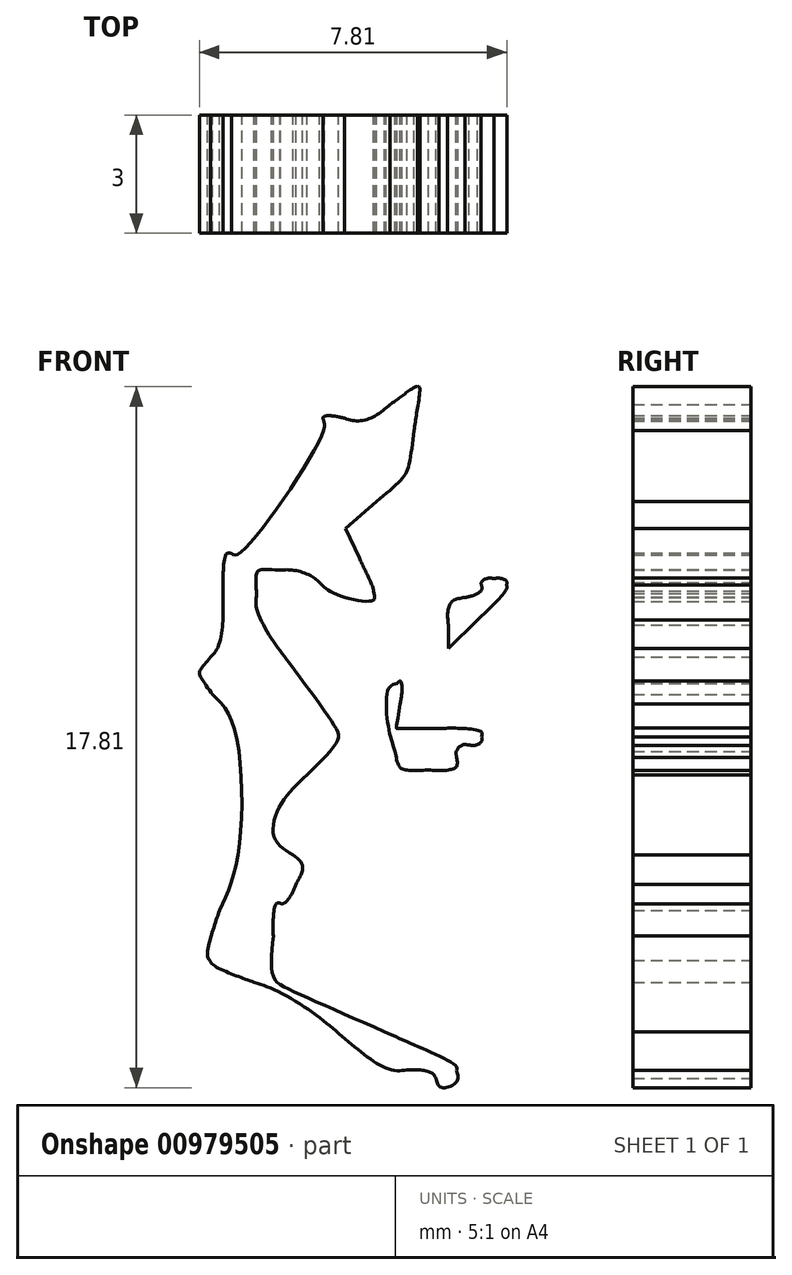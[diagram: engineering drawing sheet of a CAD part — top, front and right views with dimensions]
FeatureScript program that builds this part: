
annotation { "Feature Type Name" : "Feature", "Feature Type Description" : "" }
export const myFeature = defineFeature(function(context is Context, id is Id, definition is map)
    precondition{}
    {
        {
            var Q0;
            Q0=qCreatedBy(makeId("Front.planeOp"),FACE);
            var sketch = newSketch(context, id + "F0", { "sketchPlane" : qUnion([Q0])});
            skLineSegment(sketch, "E0", {"start": v(-32.88, 19.2) * mm, "end": v(-32.1, 20.83) * mm});
            skLineSegment(sketch, "E1", {"start": v(-32.1, 20.83) * mm, "end": v(-32.57, 22.16) * mm});
            skLineSegment(sketch, "E2", {"start": v(-27.5, 16.63) * mm, "end": v(-26.83, 16.28) * mm});
            skLineSegment(sketch, "E3", {"start": v(-26.83, 16.28) * mm, "end": v(-26.97, 16.83) * mm});
            skLineSegment(sketch, "E4", {"start": v(-24.85, 15.67) * mm, "end": v(-25.4, 15.88) * mm});
            skLineSegment(sketch, "E5", {"start": v(-25.4, 15.88) * mm, "end": v(-25.34, 18.4) * mm});
            skLineSegment(sketch, "E6", {"start": v(-1.75, 78.04) * mm, "end": v(-0.2, 79.6) * mm});
            skLineSegment(sketch, "E7", {"start": v(-0.2, 79.6) * mm, "end": v(1.27, 79.6) * mm});
            skLineSegment(sketch, "E8", {"start": v(38.3, 44.26) * mm, "end": v(38.3, 43.17) * mm});
            skLineSegment(sketch, "E9", {"start": v(38.3, 43.17) * mm, "end": v(37.62, 43.24) * mm});
            skLineSegment(sketch, "E10", {"start": v(39.65, -31.25) * mm, "end": v(39.52, -33.83) * mm});
            skLineSegment(sketch, "E11", {"start": v(39.52, -33.83) * mm, "end": v(40.18, -34.42) * mm});
            skLineSegment(sketch, "E12", {"start": v(1.4, 79.08) * mm, "end": v(0.3, 79.22) * mm});
            skLineSegment(sketch, "E13", {"start": v(0.3, 79.22) * mm, "end": v(-1.23, 77.67) * mm});
            skLineSegment(sketch, "E14", {"start": v(-12.51, 69.45) * mm, "end": v(-13.4, 69.45) * mm});
            skLineSegment(sketch, "E15", {"start": v(-13.4, 69.45) * mm, "end": v(-13.27, 67.07) * mm});
            skLineSegment(sketch, "E16", {"start": v(-18.31, 54.9) * mm, "end": v(-18.88, 53.48) * mm});
            skLineSegment(sketch, "E17", {"start": v(-18.88, 53.48) * mm, "end": v(-18.43, 53.1) * mm});
            skLineSegment(sketch, "E18", {"start": v(-20.94, 40.45) * mm, "end": v(-21.55, 40.45) * mm});
            skLineSegment(sketch, "E19", {"start": v(-21.55, 40.45) * mm, "end": v(-21.44, 41.8) * mm});
            skLineSegment(sketch, "E20", {"start": v(-24.47, 43.3) * mm, "end": v(-25.23, 42.61) * mm});
            skLineSegment(sketch, "E21", {"start": v(-25.23, 42.61) * mm, "end": v(-24.8, 41.05) * mm});
            skLineSegment(sketch, "E22", {"start": v(-37.96, -16.18) * mm, "end": v(-37.29, -17.23) * mm});
            skLineSegment(sketch, "E23", {"start": v(-37.29, -17.23) * mm, "end": v(-37.41, -20.41) * mm});
            skLineSegment(sketch, "E24", {"start": v(-30.4, -60.92) * mm, "end": v(-31.42, -62.04) * mm});
            skLineSegment(sketch, "E25", {"start": v(-31.42, -62.04) * mm, "end": v(-30.9, -63.02) * mm});
            skLineSegment(sketch, "E26", {"start": v(-36.35, 33.14) * mm, "end": v(-36.7, 33.88) * mm});
            skLineSegment(sketch, "E27", {"start": v(-36.7, 33.88) * mm, "end": v(-35.92, 34.57) * mm});
            skLineSegment(sketch, "E28", {"start": v(-34.09, 31.43) * mm, "end": v(-34.09, 30.84) * mm});
            skLineSegment(sketch, "E29", {"start": v(-34.09, 30.84) * mm, "end": v(-33.35, 31.56) * mm});
            skFitSpline(sketch, "E30", {"points": [v(-13.45, -80.7) * mm, v(-14.26, -80.4) * mm, v(-15.79, -79.86) * mm, v(-16.84, -79.51) * mm]});
            skFitSpline(sketch, "E31", {"points": [v(-16.84, -79.51) * mm, v(-20.43, -78.33) * mm, v(-20.6, -78.25) * mm, v(-21.55, -77.26) * mm]});
            skFitSpline(sketch, "E32", {"points": [v(-21.55, -77.26) * mm, v(-22.07, -76.72) * mm, v(-23.66, -74.52) * mm, v(-25.09, -72.37) * mm]});
            skFitSpline(sketch, "E33", {"points": [v(-25.09, -72.37) * mm, v(-26.52, -70.21) * mm, v(-28.36, -67.6) * mm, v(-29.19, -66.55) * mm]});
            skFitSpline(sketch, "E34", {"points": [v(-29.19, -66.55) * mm, v(-30.6, -64.76) * mm, v(-31.97, -62.53) * mm, v(-31.97, -62.03) * mm]});
            skFitSpline(sketch, "E35", {"points": [v(-31.97, -62.03) * mm, v(-31.97, -61.91) * mm, v(-31.5, -61.27) * mm, v(-30.92, -60.6) * mm]});
            skFitSpline(sketch, "E36", {"points": [v(-30.92, -60.6) * mm, v(-29.85, -59.39) * mm, v(-29, -57.92) * mm, v(-29, -57.28) * mm]});
            skFitSpline(sketch, "E37", {"points": [v(-29, -57.28) * mm, v(-29, -57.08) * mm, v(-29.34, -56.3) * mm, v(-29.75, -55.53) * mm]});
            skFitSpline(sketch, "E38", {"points": [v(-29.75, -55.53) * mm, v(-30.57, -53.98) * mm, v(-30.63, -53.57) * mm, v(-30.2, -52.72) * mm]});
            skFitSpline(sketch, "E39", {"points": [v(-30.2, -52.72) * mm, v(-29.95, -52.26) * mm, v(-29.92, -51.55) * mm, v(-30.04, -49.29) * mm]});
            skFitSpline(sketch, "E40", {"points": [v(-30.04, -49.29) * mm, v(-30.2, -46.13) * mm, v(-30.12, -46.32) * mm, v(-32.34, -43.6) * mm]});
            skFitSpline(sketch, "E41", {"points": [v(-32.34, -43.6) * mm, v(-32.83, -43) * mm, v(-33.38, -42.01) * mm, v(-33.55, -41.42) * mm]});
            skFitSpline(sketch, "E42", {"points": [v(-33.55, -41.42) * mm, v(-33.73, -40.84) * mm, v(-34.2, -39.94) * mm, v(-34.62, -39.44) * mm]});
            skFitSpline(sketch, "E43", {"points": [v(-34.62, -39.44) * mm, v(-36.03, -37.71) * mm, v(-36.52, -35.97) * mm, v(-35.98, -34.56) * mm]});
            skFitSpline(sketch, "E44", {"points": [v(-35.98, -34.56) * mm, v(-35.86, -34.24) * mm, v(-35.38, -33.57) * mm, v(-34.92, -33.07) * mm]});
            skFitSpline(sketch, "E45", {"points": [v(-34.92, -33.07) * mm, v(-33.97, -32.03) * mm, v(-34, -32.17) * mm, v(-34.37, -30.78) * mm]});
            skFitSpline(sketch, "E46", {"points": [v(-34.37, -30.78) * mm, v(-34.75, -29.38) * mm, v(-35.2, -28.53) * mm, v(-36.46, -26.88) * mm]});
            skFitSpline(sketch, "E47", {"points": [v(-36.46, -26.88) * mm, v(-37.04, -26.13) * mm, v(-37.61, -25.27) * mm, v(-37.73, -24.97) * mm]});
            skFitSpline(sketch, "E48", {"points": [v(-37.73, -24.97) * mm, v(-37.97, -24.39) * mm, v(-38.06, -21.07) * mm, v(-37.9, -18.8) * mm]});
            skFitSpline(sketch, "E49", {"points": [v(-37.9, -18.8) * mm, v(-37.82, -17.55) * mm, v(-37.87, -17.35) * mm, v(-38.39, -16.67) * mm]});
            skFitSpline(sketch, "E50", {"points": [v(-38.39, -16.67) * mm, v(-39.51, -15.19) * mm, v(-39.6, -12.77) * mm, v(-38.72, -7.81) * mm]});
            skFitSpline(sketch, "E51", {"points": [v(-38.72, -7.81) * mm, v(-38.24, -5.14) * mm, v(-38.31, -2.1) * mm, v(-38.87, -1) * mm]});
            skFitSpline(sketch, "E52", {"points": [v(-38.87, -1) * mm, v(-39.1, -0.56) * mm, v(-39.11, -0.29) * mm, v(-38.94, 0.17) * mm]});
            skFitSpline(sketch, "E53", {"points": [v(-38.94, 0.17) * mm, v(-38.62, 1) * mm, v(-38.87, 3.38) * mm, v(-39.5, 5.38) * mm]});
            skFitSpline(sketch, "E54", {"points": [v(-39.5, 5.38) * mm, v(-39.78, 6.29) * mm, v(-40.01, 7.26) * mm, v(-40.01, 7.54) * mm]});
            skFitSpline(sketch, "E55", {"points": [v(-40.01, 7.54) * mm, v(-40.01, 7.83) * mm, v(-39.68, 9.05) * mm, v(-39.27, 10.27) * mm]});
            skFitSpline(sketch, "E56", {"points": [v(-39.27, 10.27) * mm, v(-38.41, 12.85) * mm, v(-38.39, 13.06) * mm, v(-38.96, 13.2) * mm]});
            skFitSpline(sketch, "E57", {"points": [v(-38.96, 13.2) * mm, v(-39.71, 13.4) * mm, v(-39.48, 14.32) * mm, v(-38.38, 15.5) * mm]});
            skFitSpline(sketch, "E58", {"points": [v(-38.38, 15.5) * mm, v(-36.83, 17.16) * mm, v(-35.68, 17.57) * mm, v(-34.74, 16.8) * mm]});
            skFitSpline(sketch, "E59", {"points": [v(-34.74, 16.8) * mm, v(-34.08, 16.26) * mm, v(-32.77, 13.22) * mm, v(-32.66, 11.98) * mm]});
            skFitSpline(sketch, "E60", {"points": [v(-32.66, 11.98) * mm, v(-32.55, 10.86) * mm, v(-32.37, 10.61) * mm, v(-31.6, 10.6) * mm]});
            skFitSpline(sketch, "E61", {"points": [v(-31.6, 10.6) * mm, v(-31, 10.6) * mm, v(-30.96, 11.24) * mm, v(-31.55, 11.77) * mm]});
            skFitSpline(sketch, "E62", {"points": [v(-31.55, 11.77) * mm, v(-31.84, 12.03) * mm, v(-31.97, 12.42) * mm, v(-31.97, 13) * mm]});
            skFitSpline(sketch, "E63", {"points": [v(-31.97, 13) * mm, v(-31.97, 14.32) * mm, v(-32.62, 16.12) * mm, v(-33.18, 16.38) * mm]});
            skFitSpline(sketch, "E64", {"points": [v(-33.18, 16.38) * mm, v(-33.86, 16.69) * mm, v(-33.8, 17.27) * mm, v(-32.88, 19.2) * mm]});
            skFitSpline(sketch, "E65", {"points": [v(-32.57, 22.16) * mm, v(-32.82, 22.9) * mm, v(-33.03, 23.65) * mm, v(-33.03, 23.83) * mm]});
            skFitSpline(sketch, "E66", {"points": [v(-33.03, 23.83) * mm, v(-33.03, 24.1) * mm, v(-33.14, 24.14) * mm, v(-33.5, 24.01) * mm]});
            skFitSpline(sketch, "E67", {"points": [v(-33.5, 24.01) * mm, v(-33.77, 23.92) * mm, v(-34.4, 23.84) * mm, v(-34.93, 23.84) * mm]});
            skFitSpline(sketch, "E68", {"points": [v(-34.93, 23.84) * mm, v(-35.84, 23.83) * mm, v(-35.89, 23.86) * mm, v(-35.95, 24.48) * mm]});
            skFitSpline(sketch, "E69", {"points": [v(-35.95, 24.48) * mm, v(-36.05, 25.55) * mm, v(-34.78, 26.27) * mm, v(-32.78, 26.27) * mm]});
            skFitSpline(sketch, "E70", {"points": [v(-32.78, 26.27) * mm, v(-31.93, 26.27) * mm, v(-31.64, 26.16) * mm, v(-31.1, 25.65) * mm]});
            skFitSpline(sketch, "E71", {"points": [v(-31.1, 25.65) * mm, v(-30.75, 25.3) * mm, v(-30.32, 25.08) * mm, v(-30.15, 25.14) * mm]});
            skFitSpline(sketch, "E72", {"points": [v(-30.15, 25.14) * mm, v(-29.7, 25.31) * mm, v(-29.77, 25.47) * mm, v(-30.7, 26.37) * mm]});
            skFitSpline(sketch, "E73", {"points": [v(-30.7, 26.37) * mm, v(-31.5, 27.15) * mm, v(-31.55, 27.27) * mm, v(-31.55, 28.43) * mm]});
            skFitSpline(sketch, "E74", {"points": [v(-31.55, 28.43) * mm, v(-31.55, 29.6) * mm, v(-31.52, 29.65) * mm, v(-31.02, 29.65) * mm]});
            skFitSpline(sketch, "E75", {"points": [v(-31.02, 29.65) * mm, v(-30.7, 29.65) * mm, v(-30.49, 29.53) * mm, v(-30.49, 29.36) * mm]});
            skFitSpline(sketch, "E76", {"points": [v(-30.49, 29.36) * mm, v(-30.49, 28.94) * mm, v(-28.82, 27.75) * mm, v(-28.24, 27.75) * mm]});
            skFitSpline(sketch, "E77", {"points": [v(-28.24, 27.75) * mm, v(-27.83, 27.75) * mm, v(-27.75, 27.6) * mm, v(-27.62, 26.6) * mm]});
            skFitSpline(sketch, "E78", {"points": [v(-27.62, 26.6) * mm, v(-27.46, 25.26) * mm, v(-27.66, 24.55) * mm, v(-28.57, 23.22) * mm]});
            skFitSpline(sketch, "E79", {"points": [v(-28.57, 23.22) * mm, v(-29.21, 22.29) * mm, v(-29.4, 21.61) * mm, v(-29.02, 21.61) * mm]});
            skFitSpline(sketch, "E80", {"points": [v(-29.02, 21.61) * mm, v(-28.66, 21.61) * mm, v(-28.35, 20.18) * mm, v(-28.49, 19.14) * mm]});
            skFitSpline(sketch, "E81", {"points": [v(-28.49, 19.14) * mm, v(-28.66, 17.84) * mm, v(-28.36, 17.07) * mm, v(-27.5, 16.63) * mm]});
            skFitSpline(sketch, "E82", {"points": [v(-26.97, 16.83) * mm, v(-27.1, 17.33) * mm, v(-27.05, 17.38) * mm, v(-26.5, 17.38) * mm]});
            skFitSpline(sketch, "E83", {"points": [v(-26.5, 17.38) * mm, v(-25.81, 17.38) * mm, v(-25.62, 17.08) * mm, v(-25.62, 16.04) * mm]});
            skFitSpline(sketch, "E84", {"points": [v(-25.62, 16.04) * mm, v(-25.62, 15.5) * mm, v(-25.82, 15.19) * mm, v(-26.56, 14.52) * mm]});
            skFitSpline(sketch, "E85", {"points": [v(-26.56, 14.52) * mm, v(-27.09, 14.05) * mm, v(-27.58, 13.4) * mm, v(-27.66, 13.06) * mm]});
            skFitSpline(sketch, "E86", {"points": [v(-27.66, 13.06) * mm, v(-27.79, 12.49) * mm, v(-27.76, 12.45) * mm, v(-27.3, 12.58) * mm]});
            skFitSpline(sketch, "E87", {"points": [v(-27.3, 12.58) * mm, v(-27.01, 12.65) * mm, v(-26.47, 12.72) * mm, v(-26.09, 12.72) * mm]});
            skFitSpline(sketch, "E88", {"points": [v(-26.09, 12.72) * mm, v(-25.47, 12.72) * mm, v(-25.42, 12.76) * mm, v(-25.61, 13.13) * mm]});
            skFitSpline(sketch, "E89", {"points": [v(-25.61, 13.13) * mm, v(-26.02, 13.88) * mm, v(-25.88, 14.6) * mm, v(-25.31, 14.75) * mm]});
            skFitSpline(sketch, "E90", {"points": [v(-25.31, 14.75) * mm, v(-25.03, 14.82) * mm, v(-24.68, 15.01) * mm, v(-24.55, 15.17) * mm]});
            skFitSpline(sketch, "E91", {"points": [v(-24.55, 15.17) * mm, v(-24.35, 15.4) * mm, v(-24.42, 15.5) * mm, v(-24.85, 15.67) * mm]});
            skFitSpline(sketch, "E92", {"points": [v(-25.34, 18.4) * mm, v(-25.28, 20.49) * mm, v(-25.2, 21.05) * mm, v(-24.84, 21.66) * mm]});
            skFitSpline(sketch, "E93", {"points": [v(-24.84, 21.66) * mm, v(-24.6, 22.07) * mm, v(-24.33, 22.91) * mm, v(-24.25, 23.54) * mm]});
            skFitSpline(sketch, "E94", {"points": [v(-24.25, 23.54) * mm, v(-24.05, 24.98) * mm, v(-23.67, 25.42) * mm, v(-22.64, 25.42) * mm]});
            skFitSpline(sketch, "E95", {"points": [v(-22.64, 25.42) * mm, v(-21.97, 25.42) * mm, v(-21.73, 25.28) * mm, v(-21.09, 24.54) * mm]});
            skFitSpline(sketch, "E96", {"points": [v(-21.09, 24.54) * mm, v(-20.67, 24.05) * mm, v(-20.32, 23.55) * mm, v(-20.32, 23.43) * mm]});
            skFitSpline(sketch, "E97", {"points": [v(-20.32, 23.43) * mm, v(-20.3, 22.93) * mm, v(-19.5, 25.15) * mm, v(-19.5, 25.74) * mm]});
            skFitSpline(sketch, "E98", {"points": [v(-19.5, 25.74) * mm, v(-19.48, 26.68) * mm, v(-19.75, 27) * mm, v(-20.27, 26.68) * mm]});
            skFitSpline(sketch, "E99", {"points": [v(-20.27, 26.68) * mm, v(-20.84, 26.32) * mm, v(-23.7, 26.75) * mm, v(-24.99, 27.38) * mm]});
            skFitSpline(sketch, "E100", {"points": [v(-24.99, 27.38) * mm, v(-26.7, 28.23) * mm, v(-27.27, 29.95) * mm, v(-26.55, 32.07) * mm]});
            skFitSpline(sketch, "E101", {"points": [v(-26.55, 32.07) * mm, v(-26.23, 33) * mm, v(-26.23, 33.13) * mm, v(-26.58, 33.9) * mm]});
            skFitSpline(sketch, "E102", {"points": [v(-26.58, 33.9) * mm, v(-27.04, 34.91) * mm, v(-26.9, 36) * mm, v(-26.2, 36.92) * mm]});
            skFitSpline(sketch, "E103", {"points": [v(-26.2, 36.92) * mm, v(-24.96, 38.54) * mm, v(-24.76, 39.42) * mm, v(-25.3, 40.73) * mm]});
            skFitSpline(sketch, "E104", {"points": [v(-25.3, 40.73) * mm, v(-25.48, 41.15) * mm, v(-25.62, 41.87) * mm, v(-25.62, 42.33) * mm]});
            skFitSpline(sketch, "E105", {"points": [v(-25.62, 42.33) * mm, v(-25.62, 43.02) * mm, v(-25.5, 43.25) * mm, v(-24.99, 43.62) * mm]});
            skFitSpline(sketch, "E106", {"points": [v(-24.99, 43.62) * mm, v(-24.64, 43.87) * mm, v(-24.35, 44.26) * mm, v(-24.35, 44.48) * mm]});
            skFitSpline(sketch, "E107", {"points": [v(-24.35, 44.48) * mm, v(-24.35, 45.6) * mm, v(-22.43, 46.16) * mm, v(-21.62, 45.29) * mm]});
            skFitSpline(sketch, "E108", {"points": [v(-21.62, 45.29) * mm, v(-21.1, 44.74) * mm, v(-20.66, 42.78) * mm, v(-20.82, 41.8) * mm]});
            skFitSpline(sketch, "E109", {"points": [v(-20.82, 41.8) * mm, v(-20.95, 40.98) * mm, v(-20.5, 40.8) * mm, v(-20.12, 41.5) * mm]});
            skFitSpline(sketch, "E110", {"points": [v(-20.12, 41.5) * mm, v(-20, 41.74) * mm, v(-19.7, 41.93) * mm, v(-19.48, 41.93) * mm]});
            skFitSpline(sketch, "E111", {"points": [v(-19.48, 41.93) * mm, v(-19.2, 41.93) * mm, v(-19.03, 42.12) * mm, v(-18.95, 42.51) * mm]});
            skFitSpline(sketch, "E112", {"points": [v(-18.95, 42.51) * mm, v(-18.9, 42.83) * mm, v(-18.75, 43.5) * mm, v(-18.63, 44) * mm]});
            skFitSpline(sketch, "E113", {"points": [v(-18.63, 44) * mm, v(-18.15, 46.1) * mm, v(-18.46, 46.83) * mm, v(-19.95, 47.1) * mm]});
            skFitSpline(sketch, "E114", {"points": [v(-19.95, 47.1) * mm, v(-21.37, 47.35) * mm, v(-21.68, 48.31) * mm, v(-21.02, 50.45) * mm]});
            skFitSpline(sketch, "E115", {"points": [v(-21.02, 50.45) * mm, v(-20.67, 51.58) * mm, v(-20.6, 51.66) * mm, v(-20, 51.67) * mm]});
            skFitSpline(sketch, "E116", {"points": [v(-20, 51.67) * mm, v(-19.64, 51.67) * mm, v(-19.17, 51.8) * mm, v(-18.94, 51.97) * mm]});
            skFitSpline(sketch, "E117", {"points": [v(-18.94, 51.97) * mm, v(-18.56, 52.25) * mm, v(-18.55, 52.28) * mm, v(-18.9, 52.67) * mm]});
            skFitSpline(sketch, "E118", {"points": [v(-18.9, 52.67) * mm, v(-19.36, 53.18) * mm, v(-19.37, 53.99) * mm, v(-18.93, 55) * mm]});
            skFitSpline(sketch, "E119", {"points": [v(-18.93, 55) * mm, v(-18.26, 56.57) * mm, v(-18.22, 56.96) * mm, v(-18.55, 58.71) * mm]});
            skFitSpline(sketch, "E120", {"points": [v(-18.55, 58.71) * mm, v(-19.05, 61.35) * mm, v(-18.66, 63.1) * mm, v(-17.57, 63.1) * mm]});
            skFitSpline(sketch, "E121", {"points": [v(-17.57, 63.1) * mm, v(-17.13, 63.1) * mm, v(-16.93, 62.86) * mm, v(-16.62, 61.94) * mm]});
            skFitSpline(sketch, "E122", {"points": [v(-16.62, 61.94) * mm, v(-16.19, 60.62) * mm, v(-15.25, 61.36) * mm, v(-15.25, 63.03) * mm]});
            skFitSpline(sketch, "E123", {"points": [v(-15.25, 63.03) * mm, v(-15.25, 63.72) * mm, v(-15.21, 63.77) * mm, v(-14.72, 63.65) * mm]});
            skFitSpline(sketch, "E124", {"points": [v(-14.72, 63.65) * mm, v(-13.88, 63.44) * mm, v(-13.7, 64.21) * mm, v(-13.86, 67.25) * mm]});
            skFitSpline(sketch, "E125", {"points": [v(-13.86, 67.25) * mm, v(-14.01, 70.15) * mm, v(-14.06, 70.07) * mm, v(-12.21, 70.08) * mm]});
            skFitSpline(sketch, "E126", {"points": [v(-12.21, 70.08) * mm, v(-11.52, 70.08) * mm, v(-11.25, 70.23) * mm, v(-10.4, 71.12) * mm]});
            skFitSpline(sketch, "E127", {"points": [v(-10.4, 71.12) * mm, v(-9.38, 72.18) * mm, v(-9.03, 72.34) * mm, v(-6.52, 72.84) * mm]});
            skFitSpline(sketch, "E128", {"points": [v(-6.52, 72.84) * mm, v(-4.93, 73.15) * mm, v(-4.21, 73.78) * mm, v(-3.7, 75.27) * mm]});
            skFitSpline(sketch, "E129", {"points": [v(-3.7, 75.27) * mm, v(-3.38, 76.2) * mm, v(-2.96, 76.8) * mm, v(-1.75, 78.04) * mm]});
            skFitSpline(sketch, "E130", {"points": [v(1.27, 79.6) * mm, v(2.66, 79.6) * mm, v(2.79, 79.65) * mm, v(3.57, 80.36) * mm]});
            skFitSpline(sketch, "E131", {"points": [v(3.57, 80.36) * mm, v(4.72, 81.4) * mm, v(5.62, 81.51) * mm, v(6.84, 80.8) * mm]});
            skFitSpline(sketch, "E132", {"points": [v(6.84, 80.8) * mm, v(7.4, 80.48) * mm, v(8.11, 80.24) * mm, v(8.56, 80.24) * mm]});
            skFitSpline(sketch, "E133", {"points": [v(8.56, 80.24) * mm, v(9.65, 80.24) * mm, v(10.66, 79.76) * mm, v(12.03, 78.58) * mm]});
            skFitSpline(sketch, "E134", {"points": [v(12.03, 78.58) * mm, v(12.68, 78.02) * mm, v(13.76, 77.21) * mm, v(14.43, 76.8) * mm]});
            skFitSpline(sketch, "E135", {"points": [v(14.43, 76.8) * mm, v(16.07, 75.75) * mm, v(16.3, 75.23) * mm, v(16.26, 72.68) * mm]});
            skFitSpline(sketch, "E136", {"points": [v(16.26, 72.68) * mm, v(16.21, 70.3) * mm, v(16.3, 70.06) * mm, v(17.99, 67.97) * mm]});
            skFitSpline(sketch, "E137", {"points": [v(17.99, 67.97) * mm, v(19.34, 66.28) * mm, v(19.58, 65.73) * mm, v(19.78, 63.84) * mm]});
            skFitSpline(sketch, "E138", {"points": [v(19.78, 63.84) * mm, v(19.97, 61.97) * mm, v(20.1, 61.75) * mm, v(21.2, 61.28) * mm]});
            skFitSpline(sketch, "E139", {"points": [v(21.2, 61.28) * mm, v(21.95, 60.97) * mm, v(22.77, 60.9) * mm, v(25.95, 60.87) * mm]});
            skFitSpline(sketch, "E140", {"points": [v(25.95, 60.87) * mm, v(29.47, 60.83) * mm, v(29.87, 60.8) * mm, v(30.78, 60.35) * mm]});
            skFitSpline(sketch, "E141", {"points": [v(30.78, 60.35) * mm, v(31.33, 60.09) * mm, v(31.82, 59.71) * mm, v(31.88, 59.53) * mm]});
            skFitSpline(sketch, "E142", {"points": [v(31.88, 59.53) * mm, v(32.1, 58.78) * mm, v(32.32, 58.58) * mm, v(33.34, 58.19) * mm]});
            skFitSpline(sketch, "E143", {"points": [v(33.34, 58.19) * mm, v(35, 57.54) * mm, v(35.47, 56.96) * mm, v(35.61, 55.41) * mm]});
            skFitSpline(sketch, "E144", {"points": [v(35.61, 55.41) * mm, v(35.68, 54.7) * mm, v(35.93, 53.67) * mm, v(36.17, 53.15) * mm]});
            skFitSpline(sketch, "E145", {"points": [v(36.17, 53.15) * mm, v(36.4, 52.63) * mm, v(36.6, 51.94) * mm, v(36.6, 51.62) * mm]});
            skFitSpline(sketch, "E146", {"points": [v(36.6, 51.62) * mm, v(36.6, 51.3) * mm, v(36.8, 50.55) * mm, v(37.02, 49.93) * mm]});
            skFitSpline(sketch, "E147", {"points": [v(37.02, 49.93) * mm, v(37.7, 48.08) * mm, v(38.3, 45.42) * mm, v(38.3, 44.26) * mm]});
            skFitSpline(sketch, "E148", {"points": [v(37.62, 43.24) * mm, v(36.87, 43.31) * mm, v(36.86, 43.33) * mm, v(36.05, 46.9) * mm]});
            skFitSpline(sketch, "E149", {"points": [v(36.05, 46.9) * mm, v(35.75, 48.23) * mm, v(35.65, 48.45) * mm, v(35.6, 47.92) * mm]});
            skFitSpline(sketch, "E150", {"points": [v(35.6, 47.92) * mm, v(35.56, 47.55) * mm, v(35.72, 46.61) * mm, v(35.96, 45.84) * mm]});
            skFitSpline(sketch, "E151", {"points": [v(35.96, 45.84) * mm, v(36.2, 45.06) * mm, v(36.4, 44.16) * mm, v(36.4, 43.83) * mm]});
            skFitSpline(sketch, "E152", {"points": [v(36.4, 43.83) * mm, v(36.4, 42.72) * mm, v(36.23, 42.57) * mm, v(35.04, 42.57) * mm]});
            skFitSpline(sketch, "E153", {"points": [v(35.04, 42.57) * mm, v(34.35, 42.57) * mm, v(33.78, 42.44) * mm, v(33.53, 42.23) * mm]});
            skFitSpline(sketch, "E154", {"points": [v(33.53, 42.23) * mm, v(33.14, 41.92) * mm, v(33.15, 41.9) * mm, v(33.78, 42.01) * mm]});
            skFitSpline(sketch, "E155", {"points": [v(33.78, 42.01) * mm, v(34.37, 42.1) * mm, v(34.48, 42.05) * mm, v(34.7, 41.5) * mm]});
            skFitSpline(sketch, "E156", {"points": [v(34.7, 41.5) * mm, v(35.23, 40.23) * mm, v(34.46, 39.89) * mm, v(32.77, 40.66) * mm]});
            skFitSpline(sketch, "E157", {"points": [v(32.77, 40.66) * mm, v(30, 41.91) * mm, v(30.46, 40.26) * mm, v(33.3, 38.77) * mm]});
            skFitSpline(sketch, "E158", {"points": [v(33.3, 38.77) * mm, v(34.7, 38.04) * mm, v(35.03, 37.98) * mm, v(35.2, 38.44) * mm]});
            skFitSpline(sketch, "E159", {"points": [v(35.2, 38.44) * mm, v(35.4, 38.97) * mm, v(36.94, 38.86) * mm, v(37.34, 38.29) * mm]});
            skFitSpline(sketch, "E160", {"points": [v(37.34, 38.29) * mm, v(37.8, 37.64) * mm, v(37.75, 36.5) * mm, v(37.25, 35.69) * mm]});
            skFitSpline(sketch, "E161", {"points": [v(37.25, 35.69) * mm, v(37.01, 35.31) * mm, v(36.68, 34.6) * mm, v(36.5, 34.09) * mm]});
            skFitSpline(sketch, "E162", {"points": [v(36.5, 34.09) * mm, v(36.07, 32.87) * mm, v(35.62, 32.4) * mm, v(34.86, 32.4) * mm]});
            skFitSpline(sketch, "E163", {"points": [v(34.86, 32.4) * mm, v(34.06, 32.4) * mm, v(32.85, 32.98) * mm, v(32.57, 33.5) * mm]});
            skFitSpline(sketch, "E164", {"points": [v(32.57, 33.5) * mm, v(32.35, 33.9) * mm, v(32.37, 33.91) * mm, v(33.4, 34.23) * mm]});
            skFitSpline(sketch, "E165", {"points": [v(33.4, 34.23) * mm, v(33.55, 34.27) * mm, v(33.64, 34.43) * mm, v(33.6, 34.58) * mm]});
            skFitSpline(sketch, "E166", {"points": [v(33.6, 34.58) * mm, v(33.47, 34.97) * mm, v(32.1, 35.02) * mm, v(31.26, 34.66) * mm]});
            skFitSpline(sketch, "E167", {"points": [v(31.26, 34.66) * mm, v(30.63, 34.4) * mm, v(30.54, 34.27) * mm, v(30.63, 33.8) * mm]});
            skFitSpline(sketch, "E168", {"points": [v(30.63, 33.8) * mm, v(30.71, 33.37) * mm, v(30.83, 33.27) * mm, v(31.13, 33.37) * mm]});
            skFitSpline(sketch, "E169", {"points": [v(31.13, 33.37) * mm, v(31.68, 33.54) * mm, v(31.8, 33.13) * mm, v(31.57, 31.7) * mm]});
            skFitSpline(sketch, "E170", {"points": [v(31.57, 31.7) * mm, v(31.47, 31.04) * mm, v(31.4, 30.5) * mm, v(31.43, 30.5) * mm]});
            skFitSpline(sketch, "E171", {"points": [v(31.43, 30.5) * mm, v(31.46, 30.5) * mm, v(31.82, 30.65) * mm, v(32.25, 30.82) * mm]});
            skFitSpline(sketch, "E172", {"points": [v(32.25, 30.82) * mm, v(33.01, 31.14) * mm, v(33.02, 31.14) * mm, v(33.26, 30.56) * mm]});
            skFitSpline(sketch, "E173", {"points": [v(33.26, 30.56) * mm, v(33.39, 30.24) * mm, v(33.5, 29.43) * mm, v(33.52, 28.77) * mm]});
            skFitSpline(sketch, "E174", {"points": [v(33.52, 28.77) * mm, v(33.55, 27.14) * mm, v(33.03, 26.57) * mm, v(31.4, 26.43) * mm]});
            skFitSpline(sketch, "E175", {"points": [v(31.4, 26.43) * mm, v(29.99, 26.32) * mm, v(29.27, 25.83) * mm, v(28.59, 24.5) * mm]});
            skFitSpline(sketch, "E176", {"points": [v(28.59, 24.5) * mm, v(28.09, 23.52) * mm, v(28.09, 23.5) * mm, v(28.46, 22.8) * mm]});
            skFitSpline(sketch, "E177", {"points": [v(28.46, 22.8) * mm, v(29.02, 21.76) * mm, v(28.8, 20.5) * mm, v(27.76, 18.77) * mm]});
            skFitSpline(sketch, "E178", {"points": [v(27.76, 18.77) * mm, v(26.26, 16.28) * mm, v(26.34, 15.6) * mm, v(28.5, 12.89) * mm]});
            skFitSpline(sketch, "E179", {"points": [v(28.5, 12.89) * mm, v(30.07, 10.9) * mm, v(30.64, 9.85) * mm, v(31.32, 7.7) * mm]});
            skFitSpline(sketch, "E180", {"points": [v(31.32, 7.7) * mm, v(31.79, 6.2) * mm, v(31.8, 6.14) * mm, v(31.41, 5.73) * mm]});
            skFitSpline(sketch, "E181", {"points": [v(31.41, 5.73) * mm, v(31.08, 5.36) * mm, v(31.06, 5.2) * mm, v(31.28, 4.6) * mm]});
            skFitSpline(sketch, "E182", {"points": [v(31.28, 4.6) * mm, v(31.65, 3.58) * mm, v(31.59, 2.92) * mm, v(31, 1.59) * mm]});
            skFitSpline(sketch, "E183", {"points": [v(31, 1.59) * mm, v(30.4, 0.22) * mm, v(30.37, 0) * mm, v(30.73, -0.98) * mm]});
            skFitSpline(sketch, "E184", {"points": [v(30.73, -0.98) * mm, v(30.96, -1.6) * mm, v(30.93, -1.79) * mm, v(30.48, -2.62) * mm]});
            skFitSpline(sketch, "E185", {"points": [v(30.48, -2.62) * mm, v(29.76, -3.92) * mm, v(30.03, -4.4) * mm, v(31.97, -5.39) * mm]});
            skFitSpline(sketch, "E186", {"points": [v(31.97, -5.39) * mm, v(33.32, -6.07) * mm, v(33.55, -6.12) * mm, v(34.1, -5.9) * mm]});
            skFitSpline(sketch, "E187", {"points": [v(34.1, -5.9) * mm, v(34.89, -5.57) * mm, v(35.48, -5.74) * mm, v(36.67, -6.64) * mm]});
            skFitSpline(sketch, "E188", {"points": [v(36.67, -6.64) * mm, v(37.21, -7.06) * mm, v(37.94, -7.45) * mm, v(38.28, -7.52) * mm]});
            skFitSpline(sketch, "E189", {"points": [v(38.28, -7.52) * mm, v(38.74, -7.61) * mm, v(38.97, -7.82) * mm, v(39.14, -8.29) * mm]});
            skFitSpline(sketch, "E190", {"points": [v(39.14, -8.29) * mm, v(39.46, -9.22) * mm, v(39.43, -9.36) * mm, v(38.73, -10.24) * mm]});
            skFitSpline(sketch, "E191", {"points": [v(38.73, -10.24) * mm, v(37.95, -11.22) * mm, v(37.9, -12.13) * mm, v(38.57, -13.12) * mm]});
            skFitSpline(sketch, "E192", {"points": [v(38.57, -13.12) * mm, v(38.94, -13.67) * mm, v(39.23, -13.86) * mm, v(39.79, -13.91) * mm]});
            skFitSpline(sketch, "E193", {"points": [v(39.79, -13.91) * mm, v(40.2, -13.95) * mm, v(40.6, -14.1) * mm, v(40.68, -14.23) * mm]});
            skFitSpline(sketch, "E194", {"points": [v(40.68, -14.23) * mm, v(40.98, -14.7) * mm, v(40.84, -15.58) * mm, v(40.4, -15.98) * mm]});
            skFitSpline(sketch, "E195", {"points": [v(40.4, -15.98) * mm, v(40.04, -16.3) * mm, v(39.97, -16.56) * mm, v(40.05, -17.26) * mm]});
            skFitSpline(sketch, "E196", {"points": [v(40.05, -17.26) * mm, v(40.14, -18.03) * mm, v(40.09, -18.17) * mm, v(39.65, -18.37) * mm]});
            skFitSpline(sketch, "E197", {"points": [v(39.65, -18.37) * mm, v(39.06, -18.64) * mm, v(39.03, -18.9) * mm, v(39.5, -20) * mm]});
            skFitSpline(sketch, "E198", {"points": [v(39.5, -20) * mm, v(39.77, -20.67) * mm, v(39.83, -21.57) * mm, v(39.81, -24.74) * mm]});
            skFitSpline(sketch, "E199", {"points": [v(39.81, -24.74) * mm, v(39.8, -26.9) * mm, v(39.73, -29.82) * mm, v(39.65, -31.25) * mm]});
            skFitSpline(sketch, "E200", {"points": [v(40.18, -34.42) * mm, v(40.54, -34.74) * mm, v(40.84, -35.18) * mm, v(40.84, -35.41) * mm]});
            skFitSpline(sketch, "E201", {"points": [v(40.84, -35.41) * mm, v(40.84, -36.27) * mm, v(39.96, -37.65) * mm, v(38.92, -38.41) * mm]});
            skFitSpline(sketch, "E202", {"points": [v(38.92, -38.41) * mm, v(37.63, -39.36) * mm, v(37.28, -40) * mm, v(37.05, -41.89) * mm]});
            skFitSpline(sketch, "E203", {"points": [v(37.05, -41.89) * mm, v(36.94, -42.7) * mm, v(36.66, -43.77) * mm, v(36.42, -44.27) * mm]});
            skFitSpline(sketch, "E204", {"points": [v(36.42, -44.27) * mm, v(35.96, -45.22) * mm, v(33.78, -47.87) * mm, v(31.3, -50.5) * mm]});
            skFitSpline(sketch, "E205", {"points": [v(31.3, -50.5) * mm, v(29.02, -52.92) * mm, v(27.8, -55.66) * mm, v(27.2, -59.77) * mm]});
            skFitSpline(sketch, "E206", {"points": [v(27.2, -59.77) * mm, v(26.85, -62.13) * mm, v(26.75, -62.37) * mm, v(25.14, -65) * mm]});
            skFitSpline(sketch, "E207", {"points": [v(25.14, -65) * mm, v(24.58, -65.91) * mm, v(24.35, -66.6) * mm, v(24.16, -67.9) * mm]});
            skFitSpline(sketch, "E208", {"points": [v(24.16, -67.9) * mm, v(23.88, -69.93) * mm, v(23.36, -71.03) * mm, v(22.29, -71.92) * mm]});
            skFitSpline(sketch, "E209", {"points": [v(22.29, -71.92) * mm, v(21.43, -72.63) * mm, v(19.94, -73.22) * mm, v(19, -73.22) * mm]});
            skFitSpline(sketch, "E210", {"points": [v(19, -73.22) * mm, v(18.6, -73.22) * mm, v(18.4, -73.32) * mm, v(18.4, -73.56) * mm]});
            skFitSpline(sketch, "E211", {"points": [v(18.4, -73.56) * mm, v(18.4, -73.75) * mm, v(18.21, -74.22) * mm, v(17.97, -74.6) * mm]});
            skFitSpline(sketch, "E212", {"points": [v(17.97, -74.6) * mm, v(17.57, -75.26) * mm, v(17.56, -75.35) * mm, v(17.87, -76.08) * mm]});
            skFitSpline(sketch, "E213", {"points": [v(17.87, -76.08) * mm, v(18.34, -77.22) * mm, v(18.3, -77.38) * mm, v(17.14, -78.58) * mm]});
            skFitSpline(sketch, "E214", {"points": [v(17.14, -78.58) * mm, v(16.56, -79.18) * mm, v(15.87, -79.93) * mm, v(15.6, -80.25) * mm]});
            skFitSpline(sketch, "E215", {"points": [v(15.6, -80.25) * mm, v(15.34, -80.56) * mm, v(14.86, -80.88) * mm, v(14.54, -80.96) * mm]});
            skFitSpline(sketch, "E216", {"points": [v(14.54, -80.96) * mm, v(14.03, -81.08) * mm, v(13.96, -81.03) * mm, v(13.96, -80.56) * mm]});
            skFitSpline(sketch, "E217", {"points": [v(13.96, -80.56) * mm, v(13.96, -80.25) * mm, v(13.75, -79.86) * mm, v(13.47, -79.63) * mm]});
            skFitSpline(sketch, "E218", {"points": [v(13.47, -79.63) * mm, v(12.33, -78.73) * mm, v(12.3, -77.45) * mm, v(13.44, -77.45) * mm]});
            skFitSpline(sketch, "E219", {"points": [v(13.44, -77.45) * mm, v(14.2, -77.45) * mm, v(15.11, -76) * mm, v(14.94, -75.07) * mm]});
            skFitSpline(sketch, "E220", {"points": [v(14.94, -75.07) * mm, v(14.87, -74.7) * mm, v(14.75, -74.02) * mm, v(14.67, -73.57) * mm]});
            skFitSpline(sketch, "E221", {"points": [v(14.67, -73.57) * mm, v(14.58, -73.02) * mm, v(14.45, -72.8) * mm, v(14.25, -72.88) * mm]});
            skFitSpline(sketch, "E222", {"points": [v(14.25, -72.88) * mm, v(14.1, -72.94) * mm, v(13.13, -72.88) * mm, v(12.11, -72.76) * mm]});
            skFitSpline(sketch, "E223", {"points": [v(12.11, -72.76) * mm, v(10.8, -72.6) * mm, v(10.12, -72.4) * mm, v(9.8, -72.1) * mm]});
            skFitSpline(sketch, "E224", {"points": [v(9.8, -72.1) * mm, v(9.32, -71.67) * mm, v(8.88, -71.75) * mm, v(8.88, -72.28) * mm]});
            skFitSpline(sketch, "E225", {"points": [v(8.88, -72.28) * mm, v(8.88, -72.66) * mm, v(8.5, -72.65) * mm, v(7.82, -72.26) * mm]});
            skFitSpline(sketch, "E226", {"points": [v(7.82, -72.26) * mm, v(7.11, -71.86) * mm, v(5.83, -71.87) * mm, v(4.94, -72.29) * mm]});
            skFitSpline(sketch, "E227", {"points": [v(4.94, -72.29) * mm, v(4.16, -72.66) * mm, v(4.18, -72.61) * mm, v(4.14, -74.27) * mm]});
            skFitSpline(sketch, "E228", {"points": [v(4.14, -74.27) * mm, v(4.12, -75.43) * mm, v(4.11, -75.44) * mm, v(3.17, -75.91) * mm]});
            skFitSpline(sketch, "E229", {"points": [v(3.17, -75.91) * mm, v(2.65, -76.18) * mm, v(1.84, -76.77) * mm, v(1.36, -77.24) * mm]});
            skFitSpline(sketch, "E230", {"points": [v(1.36, -77.24) * mm, v(0.68, -77.91) * mm, v(-0.19, -78.37) * mm, v(-2.67, -79.37) * mm]});
            skFitSpline(sketch, "E231", {"points": [v(-2.67, -79.37) * mm, v(-6.5, -80.92) * mm, v(-7.82, -81.25) * mm, v(-10.17, -81.25) * mm]});
            skFitSpline(sketch, "E232", {"points": [v(-10.17, -81.25) * mm, v(-11.59, -81.25) * mm, v(-12.28, -81.13) * mm, v(-13.45, -80.7) * mm]});
            skFitSpline(sketch, "E233", {"points": [v(-6.84, -80.3) * mm, v(-6.29, -80.14) * mm, v(-4.56, -79.5) * mm, v(-3, -78.88) * mm]});
            skFitSpline(sketch, "E234", {"points": [v(-3, -78.88) * mm, v(-0.66, -77.96) * mm, v(0.05, -77.57) * mm, v(1.08, -76.65) * mm]});
            skFitSpline(sketch, "E235", {"points": [v(1.08, -76.65) * mm, v(1.77, -76.04) * mm, v(2.46, -75.54) * mm, v(2.62, -75.54) * mm]});
            skFitSpline(sketch, "E236", {"points": [v(2.62, -75.54) * mm, v(2.78, -75.54) * mm, v(3.12, -75.37) * mm, v(3.38, -75.16) * mm]});
            skFitSpline(sketch, "E237", {"points": [v(3.38, -75.16) * mm, v(3.8, -74.81) * mm, v(3.83, -74.72) * mm, v(3.59, -73.93) * mm]});
            skFitSpline(sketch, "E238", {"points": [v(3.59, -73.93) * mm, v(3.4, -73.28) * mm, v(3.39, -72.96) * mm, v(3.57, -72.61) * mm]});
            skFitSpline(sketch, "E239", {"points": [v(3.57, -72.61) * mm, v(4.07, -71.69) * mm, v(6.12, -71.11) * mm, v(7.53, -71.5) * mm]});
            skFitSpline(sketch, "E240", {"points": [v(7.53, -71.5) * mm, v(8.17, -71.68) * mm, v(8.4, -71.66) * mm, v(8.68, -71.41) * mm]});
            skFitSpline(sketch, "E241", {"points": [v(8.68, -71.41) * mm, v(9.15, -70.98) * mm, v(9.64, -71.02) * mm, v(10.13, -71.54) * mm]});
            skFitSpline(sketch, "E242", {"points": [v(10.13, -71.54) * mm, v(10.44, -71.88) * mm, v(10.95, -72.03) * mm, v(12.2, -72.17) * mm]});
            skFitSpline(sketch, "E243", {"points": [v(12.2, -72.17) * mm, v(13.1, -72.28) * mm, v(14, -72.32) * mm, v(14.17, -72.26) * mm]});
            skFitSpline(sketch, "E244", {"points": [v(14.17, -72.26) * mm, v(14.75, -72.09) * mm, v(15.04, -72.5) * mm, v(15.33, -73.91) * mm]});
            skFitSpline(sketch, "E245", {"points": [v(15.33, -73.91) * mm, v(15.54, -74.89) * mm, v(15.57, -75.53) * mm, v(15.43, -76.04) * mm]});
            skFitSpline(sketch, "E246", {"points": [v(15.43, -76.04) * mm, v(15.14, -77.06) * mm, v(14.45, -77.87) * mm, v(13.85, -77.87) * mm]});
            skFitSpline(sketch, "E247", {"points": [v(13.85, -77.87) * mm, v(13.06, -77.87) * mm, v(13.01, -78.27) * mm, v(13.7, -79) * mm]});
            skFitSpline(sketch, "E248", {"points": [v(13.7, -79) * mm, v(14.06, -79.37) * mm, v(14.38, -79.86) * mm, v(14.43, -80.1) * mm]});
            skFitSpline(sketch, "E249", {"points": [v(14.43, -80.1) * mm, v(14.5, -80.48) * mm, v(14.55, -80.47) * mm, v(15.03, -79.9) * mm]});
            skFitSpline(sketch, "E250", {"points": [v(15.03, -79.9) * mm, v(15.31, -79.57) * mm, v(16.02, -78.83) * mm, v(16.6, -78.28) * mm]});
            skFitSpline(sketch, "E251", {"points": [v(16.6, -78.28) * mm, v(17.64, -77.28) * mm, v(17.65, -77.26) * mm, v(17.4, -76.55) * mm]});
            skFitSpline(sketch, "E252", {"points": [v(17.4, -76.55) * mm, v(17.05, -75.6) * mm, v(17.07, -74.87) * mm, v(17.45, -74.37) * mm]});
            skFitSpline(sketch, "E253", {"points": [v(17.45, -74.37) * mm, v(17.62, -74.14) * mm, v(17.76, -73.7) * mm, v(17.76, -73.4) * mm]});
            skFitSpline(sketch, "E254", {"points": [v(17.76, -73.4) * mm, v(17.77, -72.89) * mm, v(17.86, -72.83) * mm, v(18.88, -72.7) * mm]});
            skFitSpline(sketch, "E255", {"points": [v(18.88, -72.7) * mm, v(19.5, -72.62) * mm, v(20.47, -72.3) * mm, v(21.04, -71.99) * mm]});
            skFitSpline(sketch, "E256", {"points": [v(21.04, -71.99) * mm, v(22.45, -71.22) * mm, v(23.22, -70.08) * mm, v(23.5, -68.35) * mm]});
            skFitSpline(sketch, "E257", {"points": [v(23.5, -68.35) * mm, v(23.9, -65.9) * mm, v(24.16, -65.2) * mm, v(25.1, -63.87) * mm]});
            skFitSpline(sketch, "E258", {"points": [v(25.1, -63.87) * mm, v(26.18, -62.33) * mm, v(26.35, -61.85) * mm, v(26.67, -59.46) * mm]});
            skFitSpline(sketch, "E259", {"points": [v(26.67, -59.46) * mm, v(26.98, -57.13) * mm, v(27.93, -54.18) * mm, v(28.89, -52.58) * mm]});
            skFitSpline(sketch, "E260", {"points": [v(28.89, -52.58) * mm, v(29.3, -51.88) * mm, v(30.25, -50.69) * mm, v(31, -49.93) * mm]});
            skFitSpline(sketch, "E261", {"points": [v(31, -49.93) * mm, v(33.26, -47.61) * mm, v(35.36, -45.01) * mm, v(35.9, -43.88) * mm]});
            skFitSpline(sketch, "E262", {"points": [v(35.9, -43.88) * mm, v(36.17, -43.28) * mm, v(36.49, -42.11) * mm, v(36.6, -41.27) * mm]});
            skFitSpline(sketch, "E263", {"points": [v(36.6, -41.27) * mm, v(36.81, -39.5) * mm, v(37.06, -39.06) * mm, v(38.37, -38.07) * mm]});
            skFitSpline(sketch, "E264", {"points": [v(38.37, -38.07) * mm, v(39.26, -37.4) * mm, v(40.2, -36.1) * mm, v(40.2, -35.57) * mm]});
            skFitSpline(sketch, "E265", {"points": [v(40.2, -35.57) * mm, v(40.2, -35.45) * mm, v(39.98, -35.11) * mm, v(39.7, -34.83) * mm]});
            skFitSpline(sketch, "E266", {"points": [v(39.7, -34.83) * mm, v(38.98, -34.12) * mm, v(38.86, -33.18) * mm, v(39.13, -30.68) * mm]});
            skFitSpline(sketch, "E267", {"points": [v(39.13, -30.68) * mm, v(39.26, -29.5) * mm, v(39.36, -26.93) * mm, v(39.36, -24.95) * mm]});
            skFitSpline(sketch, "E268", {"points": [v(39.36, -24.95) * mm, v(39.36, -21.87) * mm, v(39.3, -21.22) * mm, v(38.94, -20.3) * mm]});
            skFitSpline(sketch, "E269", {"points": [v(38.94, -20.3) * mm, v(38.39, -18.9) * mm, v(38.4, -18.51) * mm, v(39.04, -18) * mm]});
            skFitSpline(sketch, "E270", {"points": [v(39.04, -18) * mm, v(39.45, -17.69) * mm, v(39.57, -17.4) * mm, v(39.57, -16.76) * mm]});
            skFitSpline(sketch, "E271", {"points": [v(39.57, -16.76) * mm, v(39.57, -16.2) * mm, v(39.7, -15.8) * mm, v(39.97, -15.56) * mm]});
            skFitSpline(sketch, "E272", {"points": [v(39.97, -15.56) * mm, v(40.59, -15) * mm, v(40.32, -14.37) * mm, v(39.46, -14.37) * mm]});
            skFitSpline(sketch, "E273", {"points": [v(39.46, -14.37) * mm, v(38.38, -14.37) * mm, v(37.67, -13.4) * mm, v(37.67, -11.9) * mm]});
            skFitSpline(sketch, "E274", {"points": [v(37.67, -11.9) * mm, v(37.67, -10.72) * mm, v(37.93, -9.95) * mm, v(38.44, -9.65) * mm]});
            skFitSpline(sketch, "E275", {"points": [v(38.44, -9.65) * mm, v(39.04, -9.3) * mm, v(38.7, -8.02) * mm, v(38, -8.02) * mm]});
            skFitSpline(sketch, "E276", {"points": [v(38, -8.02) * mm, v(37.74, -8.02) * mm, v(37, -7.64) * mm, v(36.34, -7.18) * mm]});
            skFitSpline(sketch, "E277", {"points": [v(36.34, -7.18) * mm, v(35.18, -6.34) * mm, v(34.43, -6.12) * mm, v(34.18, -6.54) * mm]});
            skFitSpline(sketch, "E278", {"points": [v(34.18, -6.54) * mm, v(34.1, -6.66) * mm, v(33.87, -6.75) * mm, v(33.65, -6.75) * mm]});
            skFitSpline(sketch, "E279", {"points": [v(33.65, -6.75) * mm, v(33.07, -6.75) * mm, v(30.08, -5.09) * mm, v(29.83, -4.63) * mm]});
            skFitSpline(sketch, "E280", {"points": [v(29.83, -4.63) * mm, v(29.5, -4) * mm, v(29.6, -2.89) * mm, v(30.04, -2.22) * mm]});
            skFitSpline(sketch, "E281", {"points": [v(30.04, -2.22) * mm, v(30.4, -1.66) * mm, v(30.41, -1.54) * mm, v(30.14, -1.01) * mm]});
            skFitSpline(sketch, "E282", {"points": [v(30.14, -1.01) * mm, v(29.71, -0.19) * mm, v(29.76, 0.38) * mm, v(30.37, 1.68) * mm]});
            skFitSpline(sketch, "E283", {"points": [v(30.37, 1.68) * mm, v(30.96, 2.95) * mm, v(31, 3.5) * mm, v(30.65, 4.7) * mm]});
            skFitSpline(sketch, "E284", {"points": [v(30.65, 4.7) * mm, v(30.44, 5.4) * mm, v(30.46, 5.58) * mm, v(30.78, 5.93) * mm]});
            skFitSpline(sketch, "E285", {"points": [v(30.78, 5.93) * mm, v(31.13, 6.33) * mm, v(31.13, 6.4) * mm, v(30.68, 7.79) * mm]});
            skFitSpline(sketch, "E286", {"points": [v(30.68, 7.79) * mm, v(30.01, 9.8) * mm, v(29.64, 10.47) * mm, v(28.1, 12.43) * mm]});
            skFitSpline(sketch, "E287", {"points": [v(28.1, 12.43) * mm, v(27.35, 13.37) * mm, v(26.61, 14.44) * mm, v(26.46, 14.8) * mm]});
            skFitSpline(sketch, "E288", {"points": [v(26.46, 14.8) * mm, v(26, 15.95) * mm, v(26.28, 17.5) * mm, v(27.26, 19.16) * mm]});
            skFitSpline(sketch, "E289", {"points": [v(27.26, 19.16) * mm, v(28.4, 21.1) * mm, v(28.53, 21.7) * mm, v(27.93, 22.5) * mm]});
            skFitSpline(sketch, "E290", {"points": [v(27.93, 22.5) * mm, v(27.4, 23.23) * mm, v(27.46, 23.77) * mm, v(28.28, 25.17) * mm]});
            skFitSpline(sketch, "E291", {"points": [v(28.28, 25.17) * mm, v(28.94, 26.3) * mm, v(29.89, 26.9) * mm, v(31.02, 26.9) * mm]});
            skFitSpline(sketch, "E292", {"points": [v(31.02, 26.9) * mm, v(31.6, 26.9) * mm, v(32.1, 27.06) * mm, v(32.48, 27.36) * mm]});
            skFitSpline(sketch, "E293", {"points": [v(32.48, 27.36) * mm, v(33, 27.78) * mm, v(33.05, 27.91) * mm, v(32.96, 28.95) * mm]});
            skFitSpline(sketch, "E294", {"points": [v(32.96, 28.95) * mm, v(32.91, 29.57) * mm, v(32.82, 30.13) * mm, v(32.76, 30.19) * mm]});
            skFitSpline(sketch, "E295", {"points": [v(32.76, 30.19) * mm, v(32.7, 30.25) * mm, v(32.3, 30.15) * mm, v(31.89, 29.97) * mm]});
            skFitSpline(sketch, "E296", {"points": [v(31.89, 29.97) * mm, v(31.46, 29.8) * mm, v(31.06, 29.65) * mm, v(30.98, 29.65) * mm]});
            skFitSpline(sketch, "E297", {"points": [v(30.98, 29.65) * mm, v(30.9, 29.65) * mm, v(30.9, 30.37) * mm, v(30.97, 31.24) * mm]});
            skFitSpline(sketch, "E298", {"points": [v(30.97, 31.24) * mm, v(31.1, 32.73) * mm, v(31.07, 32.83) * mm, v(30.68, 32.83) * mm]});
            skFitSpline(sketch, "E299", {"points": [v(30.68, 32.83) * mm, v(30.45, 32.83) * mm, v(30.26, 32.97) * mm, v(30.26, 33.15) * mm]});
            skFitSpline(sketch, "E300", {"points": [v(30.26, 33.15) * mm, v(30.26, 33.32) * mm, v(30.16, 33.46) * mm, v(30.05, 33.46) * mm]});
            skFitSpline(sketch, "E301", {"points": [v(30.05, 33.46) * mm, v(29.69, 33.46) * mm, v(29.82, 34.44) * mm, v(30.23, 34.81) * mm]});
            skFitSpline(sketch, "E302", {"points": [v(30.23, 34.81) * mm, v(30.44, 35) * mm, v(31.16, 35.28) * mm, v(31.83, 35.42) * mm]});
            skFitSpline(sketch, "E303", {"points": [v(31.83, 35.42) * mm, v(32.85, 35.63) * mm, v(33.13, 35.62) * mm, v(33.6, 35.36) * mm]});
            skFitSpline(sketch, "E304", {"points": [v(33.6, 35.36) * mm, v(34.37, 34.93) * mm, v(34.48, 34.05) * mm, v(33.82, 33.73) * mm]});
            skFitSpline(sketch, "E305", {"points": [v(33.82, 33.73) * mm, v(33.34, 33.51) * mm, v(33.35, 33.5) * mm, v(34.15, 33.16) * mm]});
            skFitSpline(sketch, "E306", {"points": [v(34.15, 33.16) * mm, v(34.9, 32.83) * mm, v(34.99, 32.83) * mm, v(35.36, 33.17) * mm]});
            skFitSpline(sketch, "E307", {"points": [v(35.36, 33.17) * mm, v(35.58, 33.37) * mm, v(35.76, 33.64) * mm, v(35.76, 33.77) * mm]});
            skFitSpline(sketch, "E308", {"points": [v(35.76, 33.77) * mm, v(35.76, 33.9) * mm, v(36.1, 34.7) * mm, v(36.5, 35.56) * mm]});
            skFitSpline(sketch, "E309", {"points": [v(36.5, 35.56) * mm, v(37.29, 37.18) * mm, v(37.3, 37.75) * mm, v(36.61, 38.12) * mm]});
            skFitSpline(sketch, "E310", {"points": [v(36.61, 38.12) * mm, v(36.14, 38.38) * mm, v(35.55, 38.19) * mm, v(35.55, 37.78) * mm]});
            skFitSpline(sketch, "E311", {"points": [v(35.55, 37.78) * mm, v(35.55, 36.66) * mm, v(30.79, 39.12) * mm, v(30.36, 40.45) * mm]});
            skFitSpline(sketch, "E312", {"points": [v(30.36, 40.45) * mm, v(30.3, 40.68) * mm, v(30.34, 41.05) * mm, v(30.47, 41.29) * mm]});
            skFitSpline(sketch, "E313", {"points": [v(30.47, 41.29) * mm, v(30.77, 41.86) * mm, v(31.55, 41.83) * mm, v(33.01, 41.2) * mm]});
            skFitSpline(sketch, "E314", {"points": [v(33.01, 41.2) * mm, v(34.25, 40.67) * mm, v(34.4, 40.66) * mm, v(34.2, 41.18) * mm]});
            skFitSpline(sketch, "E315", {"points": [v(34.2, 41.18) * mm, v(34.13, 41.4) * mm, v(33.81, 41.5) * mm, v(33.34, 41.5) * mm]});
            skFitSpline(sketch, "E316", {"points": [v(33.34, 41.5) * mm, v(32.48, 41.5) * mm, v(32.37, 41.83) * mm, v(32.97, 42.57) * mm]});
            skFitSpline(sketch, "E317", {"points": [v(32.97, 42.57) * mm, v(33.3, 42.96) * mm, v(33.56, 43.04) * mm, v(34.54, 43.04) * mm]});
            skFitSpline(sketch, "E318", {"points": [v(34.54, 43.04) * mm, v(36.05, 43.02) * mm, v(36.12, 43.25) * mm, v(35.4, 45.67) * mm]});
            skFitSpline(sketch, "E319", {"points": [v(35.4, 45.67) * mm, v(34.98, 47.1) * mm, v(34.9, 47.7) * mm, v(35.01, 48.62) * mm]});
            skFitSpline(sketch, "E320", {"points": [v(35.01, 48.62) * mm, v(35.1, 49.37) * mm, v(35.26, 49.76) * mm, v(35.45, 49.76) * mm]});
            skFitSpline(sketch, "E321", {"points": [v(35.45, 49.76) * mm, v(35.79, 49.76) * mm, v(36.46, 48.04) * mm, v(36.81, 46.27) * mm]});
            skFitSpline(sketch, "E322", {"points": [v(36.81, 46.27) * mm, v(37.15, 44.53) * mm, v(37.45, 43.62) * mm, v(37.68, 43.62) * mm]});
            skFitSpline(sketch, "E323", {"points": [v(37.68, 43.62) * mm, v(37.8, 43.62) * mm, v(37.88, 43.84) * mm, v(37.88, 44.1) * mm]});
            skFitSpline(sketch, "E324", {"points": [v(37.88, 44.1) * mm, v(37.88, 44.74) * mm, v(36.88, 48.83) * mm, v(36.6, 49.36) * mm]});
            skFitSpline(sketch, "E325", {"points": [v(36.6, 49.36) * mm, v(36.47, 49.6) * mm, v(36.29, 50.3) * mm, v(36.19, 50.92) * mm]});
            skFitSpline(sketch, "E326", {"points": [v(36.19, 50.92) * mm, v(36.09, 51.54) * mm, v(35.8, 52.48) * mm, v(35.57, 53.01) * mm]});
            skFitSpline(sketch, "E327", {"points": [v(35.57, 53.01) * mm, v(35.31, 53.57) * mm, v(35.13, 54.41) * mm, v(35.13, 55.03) * mm]});
            skFitSpline(sketch, "E328", {"points": [v(35.13, 55.03) * mm, v(35.13, 56.37) * mm, v(34.52, 57.14) * mm, v(33.05, 57.66) * mm]});
            skFitSpline(sketch, "E329", {"points": [v(33.05, 57.66) * mm, v(31.97, 58.05) * mm, v(31.44, 58.5) * mm, v(31.02, 59.34) * mm]});
            skFitSpline(sketch, "E330", {"points": [v(31.02, 59.34) * mm, v(30.64, 60.08) * mm, v(29.4, 60.31) * mm, v(25.6, 60.34) * mm]});
            skFitSpline(sketch, "E331", {"points": [v(25.6, 60.34) * mm, v(21.36, 60.37) * mm, v(20.2, 60.66) * mm, v(19.62, 61.83) * mm]});
            skFitSpline(sketch, "E332", {"points": [v(19.62, 61.83) * mm, v(19.42, 62.24) * mm, v(19.25, 63.05) * mm, v(19.25, 63.63) * mm]});
            skFitSpline(sketch, "E333", {"points": [v(19.25, 63.63) * mm, v(19.24, 64.97) * mm, v(18.71, 66.14) * mm, v(17.39, 67.73) * mm]});
            skFitSpline(sketch, "E334", {"points": [v(17.39, 67.73) * mm, v(15.95, 69.45) * mm, v(15.56, 70.55) * mm, v(15.72, 72.4) * mm]});
            skFitSpline(sketch, "E335", {"points": [v(15.72, 72.4) * mm, v(15.89, 74.42) * mm, v(15.61, 75.26) * mm, v(14.57, 75.97) * mm]});
            skFitSpline(sketch, "E336", {"points": [v(14.57, 75.97) * mm, v(13.8, 76.48) * mm, v(12.94, 77.13) * mm, v(10.52, 78.96) * mm]});
            skFitSpline(sketch, "E337", {"points": [v(10.52, 78.96) * mm, v(9.93, 79.4) * mm, v(9.37, 79.6) * mm, v(8.4, 79.72) * mm]});
            skFitSpline(sketch, "E338", {"points": [v(8.4, 79.72) * mm, v(7.67, 79.8) * mm, v(6.83, 80.05) * mm, v(6.52, 80.27) * mm]});
            skFitSpline(sketch, "E339", {"points": [v(6.52, 80.27) * mm, v(5.73, 80.83) * mm, v(4.99, 80.76) * mm, v(4.18, 80.06) * mm]});
            skFitSpline(sketch, "E340", {"points": [v(4.18, 80.06) * mm, v(3.06, 79.09) * mm, v(2.62, 78.93) * mm, v(1.4, 79.08) * mm]});
            skFitSpline(sketch, "E341", {"points": [v(-1.23, 77.67) * mm, v(-2.35, 76.53) * mm, v(-2.88, 75.8) * mm, v(-3.2, 74.95) * mm]});
            skFitSpline(sketch, "E342", {"points": [v(-3.2, 74.95) * mm, v(-3.44, 74.31) * mm, v(-3.84, 73.58) * mm, v(-4.08, 73.32) * mm]});
            skFitSpline(sketch, "E343", {"points": [v(-4.08, 73.32) * mm, v(-4.6, 72.75) * mm, v(-5.86, 72.28) * mm, v(-7.31, 72.1) * mm]});
            skFitSpline(sketch, "E344", {"points": [v(-7.31, 72.1) * mm, v(-8.5, 71.94) * mm, v(-9.16, 71.58) * mm, v(-9.92, 70.68) * mm]});
            skFitSpline(sketch, "E345", {"points": [v(-9.92, 70.68) * mm, v(-10.62, 69.85) * mm, v(-11.46, 69.45) * mm, v(-12.51, 69.45) * mm]});
            skFitSpline(sketch, "E346", {"points": [v(-13.27, 67.07) * mm, v(-13.12, 64.4) * mm, v(-13.35, 63.34) * mm, v(-14.15, 63) * mm]});
            skFitSpline(sketch, "E347", {"points": [v(-14.15, 63) * mm, v(-14.41, 62.88) * mm, v(-14.68, 62.54) * mm, v(-14.74, 62.25) * mm]});
            skFitSpline(sketch, "E348", {"points": [v(-14.74, 62.25) * mm, v(-14.95, 61.27) * mm, v(-15.22, 60.8) * mm, v(-15.67, 60.66) * mm]});
            skFitSpline(sketch, "E349", {"points": [v(-15.67, 60.66) * mm, v(-16.3, 60.47) * mm, v(-17.15, 61.07) * mm, v(-17.15, 61.71) * mm]});
            skFitSpline(sketch, "E350", {"points": [v(-17.15, 61.71) * mm, v(-17.15, 62.4) * mm, v(-17.57, 62.62) * mm, v(-17.95, 62.12) * mm]});
            skFitSpline(sketch, "E351", {"points": [v(-17.95, 62.12) * mm, v(-18.25, 61.72) * mm, v(-18.24, 60.86) * mm, v(-17.87, 57.55) * mm]});
            skFitSpline(sketch, "E352", {"points": [v(-17.87, 57.55) * mm, v(-17.76, 56.53) * mm, v(-17.83, 56.11) * mm, v(-18.31, 54.9) * mm]});
            skFitSpline(sketch, "E353", {"points": [v(-18.43, 53.1) * mm, v(-18.09, 52.84) * mm, v(-18, 52.61) * mm, v(-18.12, 52.26) * mm]});
            skFitSpline(sketch, "E354", {"points": [v(-18.12, 52.26) * mm, v(-18.35, 51.5) * mm, v(-18.6, 51.29) * mm, v(-19.44, 51.14) * mm]});
            skFitSpline(sketch, "E355", {"points": [v(-19.44, 51.14) * mm, v(-20.16, 51.02) * mm, v(-20.25, 50.92) * mm, v(-20.59, 49.92) * mm]});
            skFitSpline(sketch, "E356", {"points": [v(-20.59, 49.92) * mm, v(-21.07, 48.49) * mm, v(-20.79, 47.82) * mm, v(-19.64, 47.63) * mm]});
            skFitSpline(sketch, "E357", {"points": [v(-19.64, 47.63) * mm, v(-18.7, 47.48) * mm, v(-18.1, 46.98) * mm, v(-17.9, 46.22) * mm]});
            skFitSpline(sketch, "E358", {"points": [v(-17.9, 46.22) * mm, v(-17.82, 45.92) * mm, v(-17.92, 44.77) * mm, v(-18.12, 43.68) * mm]});
            skFitSpline(sketch, "E359", {"points": [v(-18.12, 43.68) * mm, v(-18.44, 41.9) * mm, v(-18.54, 41.66) * mm, v(-19.03, 41.44) * mm]});
            skFitSpline(sketch, "E360", {"points": [v(-19.03, 41.44) * mm, v(-19.33, 41.3) * mm, v(-19.75, 41.02) * mm, v(-19.96, 40.82) * mm]});
            skFitSpline(sketch, "E361", {"points": [v(-19.96, 40.82) * mm, v(-20.16, 40.62) * mm, v(-20.6, 40.45) * mm, v(-20.94, 40.45) * mm]});
            skFitSpline(sketch, "E362", {"points": [v(-21.44, 41.8) * mm, v(-21.32, 43.27) * mm, v(-21.6, 44.43) * mm, v(-22.21, 44.98) * mm]});
            skFitSpline(sketch, "E363", {"points": [v(-22.21, 44.98) * mm, v(-22.54, 45.28) * mm, v(-22.7, 45.3) * mm, v(-23.16, 45.08) * mm]});
            skFitSpline(sketch, "E364", {"points": [v(-23.16, 45.08) * mm, v(-23.48, 44.93) * mm, v(-23.72, 44.65) * mm, v(-23.72, 44.41) * mm]});
            skFitSpline(sketch, "E365", {"points": [v(-23.72, 44.41) * mm, v(-23.72, 44.19) * mm, v(-24.06, 43.69) * mm, v(-24.47, 43.3) * mm]});
            skFitSpline(sketch, "E366", {"points": [v(-24.8, 41.05) * mm, v(-24.28, 39.2) * mm, v(-24.4, 38.43) * mm, v(-25.38, 37) * mm]});
            skFitSpline(sketch, "E367", {"points": [v(-25.38, 37) * mm, v(-26.38, 35.55) * mm, v(-26.52, 35.03) * mm, v(-26.15, 34.3) * mm]});
            skFitSpline(sketch, "E368", {"points": [v(-26.15, 34.3) * mm, v(-25.74, 33.52) * mm, v(-25.75, 32.64) * mm, v(-26.17, 31.34) * mm]});
            skFitSpline(sketch, "E369", {"points": [v(-26.17, 31.34) * mm, v(-26.5, 30.34) * mm, v(-26.5, 30.27) * mm, v(-26.05, 29.35) * mm]});
            skFitSpline(sketch, "E370", {"points": [v(-26.05, 29.35) * mm, v(-25.45, 28.12) * mm, v(-24.64, 27.64) * mm, v(-22.5, 27.27) * mm]});
            skFitSpline(sketch, "E371", {"points": [v(-22.5, 27.27) * mm, v(-21.03, 27.01) * mm, v(-20.71, 27.01) * mm, v(-20.51, 27.25) * mm]});
            skFitSpline(sketch, "E372", {"points": [v(-20.51, 27.25) * mm, v(-20.2, 27.62) * mm, v(-19.6, 27.62) * mm, v(-19.29, 27.24) * mm]});
            skFitSpline(sketch, "E373", {"points": [v(-19.29, 27.24) * mm, v(-18.74, 26.58) * mm, v(-18.77, 25.45) * mm, v(-19.37, 23.93) * mm]});
            skFitSpline(sketch, "E374", {"points": [v(-19.37, 23.93) * mm, v(-19.7, 23.08) * mm, v(-20.07, 22.46) * mm, v(-20.24, 22.46) * mm]});
            skFitSpline(sketch, "E375", {"points": [v(-20.24, 22.46) * mm, v(-20.4, 22.46) * mm, v(-20.54, 22.54) * mm, v(-20.54, 22.65) * mm]});
            skFitSpline(sketch, "E376", {"points": [v(-20.54, 22.65) * mm, v(-20.54, 23.08) * mm, v(-22.27, 25) * mm, v(-22.65, 25) * mm]});
            skFitSpline(sketch, "E377", {"points": [v(-22.65, 25) * mm, v(-23.23, 25) * mm, v(-23.72, 24.2) * mm, v(-23.72, 23.22) * mm]});
            skFitSpline(sketch, "E378", {"points": [v(-23.72, 23.22) * mm, v(-23.72, 22.72) * mm, v(-23.92, 22.04) * mm, v(-24.24, 21.5) * mm]});
            skFitSpline(sketch, "E379", {"points": [v(-24.24, 21.5) * mm, v(-24.66, 20.79) * mm, v(-24.75, 20.34) * mm, v(-24.74, 19.26) * mm]});
            skFitSpline(sketch, "E380", {"points": [v(-24.74, 19.26) * mm, v(-24.72, 18.51) * mm, v(-24.78, 17.69) * mm, v(-24.86, 17.43) * mm]});
            skFitSpline(sketch, "E381", {"points": [v(-24.86, 17.43) * mm, v(-25.08, 16.75) * mm, v(-24.82, 16.1) * mm, v(-24.33, 16.1) * mm]});
            skFitSpline(sketch, "E382", {"points": [v(-24.33, 16.1) * mm, v(-23.36, 16.1) * mm, v(-23.83, 14.55) * mm, v(-24.88, 14.3) * mm]});
            skFitSpline(sketch, "E383", {"points": [v(-24.88, 14.3) * mm, v(-25.3, 14.18) * mm, v(-25.36, 14.09) * mm, v(-25.2, 13.77) * mm]});
            skFitSpline(sketch, "E384", {"points": [v(-25.2, 13.77) * mm, v(-24.96, 13.34) * mm, v(-24.91, 12.23) * mm, v(-25.11, 12.03) * mm]});
            skFitSpline(sketch, "E385", {"points": [v(-25.11, 12.03) * mm, v(-25.18, 11.96) * mm, v(-25.46, 11.98) * mm, v(-25.73, 12.09) * mm]});
            skFitSpline(sketch, "E386", {"points": [v(-25.73, 12.09) * mm, v(-26.03, 12.2) * mm, v(-26.5, 12.18) * mm, v(-26.98, 12.04) * mm]});
            skFitSpline(sketch, "E387", {"points": [v(-26.98, 12.04) * mm, v(-28.78, 11.48) * mm, v(-28.79, 13.48) * mm, v(-26.99, 14.98) * mm]});
            skFitSpline(sketch, "E388", {"points": [v(-26.99, 14.98) * mm, v(-26.47, 15.42) * mm, v(-26.04, 15.92) * mm, v(-26.04, 16.09) * mm]});
            skFitSpline(sketch, "E389", {"points": [v(-26.04, 16.09) * mm, v(-26.04, 16.33) * mm, v(-26.1, 16.35) * mm, v(-26.3, 16.15) * mm]});
            skFitSpline(sketch, "E390", {"points": [v(-26.3, 16.15) * mm, v(-26.76, 15.69) * mm, v(-27.73, 15.86) * mm, v(-28.39, 16.52) * mm]});
            skFitSpline(sketch, "E391", {"points": [v(-28.39, 16.52) * mm, v(-28.98, 17.1) * mm, v(-29, 17.22) * mm, v(-29, 18.97) * mm]});
            skFitSpline(sketch, "E392", {"points": [v(-29, 18.97) * mm, v(-29, 20.63) * mm, v(-29.05, 20.82) * mm, v(-29.43, 20.91) * mm]});
            skFitSpline(sketch, "E393", {"points": [v(-29.43, 20.91) * mm, v(-30.19, 21.11) * mm, v(-29.94, 22.23) * mm, v(-28.69, 24.26) * mm]});
            skFitSpline(sketch, "E394", {"points": [v(-28.69, 24.26) * mm, v(-27.87, 25.58) * mm, v(-28, 27.33) * mm, v(-28.9, 27.33) * mm]});
            skFitSpline(sketch, "E395", {"points": [v(-28.9, 27.33) * mm, v(-29.17, 27.33) * mm, v(-29.7, 27.61) * mm, v(-30.07, 27.96) * mm]});
            skFitSpline(sketch, "E396", {"points": [v(-30.07, 27.96) * mm, v(-30.87, 28.71) * mm, v(-31.12, 28.76) * mm, v(-31.12, 28.14) * mm]});
            skFitSpline(sketch, "E397", {"points": [v(-31.12, 28.14) * mm, v(-31.12, 27.9) * mm, v(-30.7, 27.23) * mm, v(-30.17, 26.67) * mm]});
            skFitSpline(sketch, "E398", {"points": [v(-30.17, 26.67) * mm, v(-29.12, 25.55) * mm, v(-29.07, 25.4) * mm, v(-29.55, 24.9) * mm]});
            skFitSpline(sketch, "E399", {"points": [v(-29.55, 24.9) * mm, v(-30.1, 24.36) * mm, v(-30.96, 24.5) * mm, v(-31.6, 25.23) * mm]});
            skFitSpline(sketch, "E400", {"points": [v(-31.6, 25.23) * mm, v(-32.15, 25.85) * mm, v(-32.25, 25.88) * mm, v(-33.19, 25.74) * mm]});
            skFitSpline(sketch, "E401", {"points": [v(-33.19, 25.74) * mm, v(-34.37, 25.57) * mm, v(-35.26, 25.15) * mm, v(-35.43, 24.68) * mm]});
            skFitSpline(sketch, "E402", {"points": [v(-35.43, 24.68) * mm, v(-35.6, 24.23) * mm, v(-35.14, 24.08) * mm, v(-34.43, 24.35) * mm]});
            skFitSpline(sketch, "E403", {"points": [v(-34.43, 24.35) * mm, v(-34.1, 24.48) * mm, v(-33.54, 24.57) * mm, v(-33.15, 24.57) * mm]});
            skFitSpline(sketch, "E404", {"points": [v(-33.15, 24.57) * mm, v(-32.54, 24.57) * mm, v(-32.46, 24.5) * mm, v(-32.44, 24) * mm]});
            skFitSpline(sketch, "E405", {"points": [v(-32.44, 24) * mm, v(-32.43, 23.67) * mm, v(-32.27, 23.06) * mm, v(-32.1, 22.62) * mm]});
            skFitSpline(sketch, "E406", {"points": [v(-32.1, 22.62) * mm, v(-31.58, 21.42) * mm, v(-31.67, 20.28) * mm, v(-32.4, 18.86) * mm]});
            skFitSpline(sketch, "E407", {"points": [v(-32.4, 18.86) * mm, v(-33.14, 17.4) * mm, v(-33.17, 17.05) * mm, v(-32.63, 16.75) * mm]});
            skFitSpline(sketch, "E408", {"points": [v(-32.63, 16.75) * mm, v(-32.1, 16.47) * mm, v(-31.55, 14.82) * mm, v(-31.55, 13.54) * mm]});
            skFitSpline(sketch, "E409", {"points": [v(-31.55, 13.54) * mm, v(-31.55, 12.77) * mm, v(-31.45, 12.46) * mm, v(-31.11, 12.23) * mm]});
            skFitSpline(sketch, "E410", {"points": [v(-31.11, 12.23) * mm, v(-30.88, 12.06) * mm, v(-30.63, 11.6) * mm, v(-30.56, 11.18) * mm]});
            skFitSpline(sketch, "E411", {"points": [v(-30.56, 11.18) * mm, v(-30.46, 10.56) * mm, v(-30.52, 10.4) * mm, v(-30.91, 10.18) * mm]});
            skFitSpline(sketch, "E412", {"points": [v(-30.91, 10.18) * mm, v(-31.53, 9.85) * mm, v(-32.75, 10.1) * mm, v(-33.03, 10.6) * mm]});
            skFitSpline(sketch, "E413", {"points": [v(-33.03, 10.6) * mm, v(-33.14, 10.82) * mm, v(-33.25, 11.41) * mm, v(-33.26, 11.91) * mm]});
            skFitSpline(sketch, "E414", {"points": [v(-33.26, 11.91) * mm, v(-33.27, 12.53) * mm, v(-33.55, 13.4) * mm, v(-34.16, 14.63) * mm]});
            skFitSpline(sketch, "E415", {"points": [v(-34.16, 14.63) * mm, v(-34.97, 16.28) * mm, v(-35.1, 16.43) * mm, v(-35.72, 16.5) * mm]});
            skFitSpline(sketch, "E416", {"points": [v(-35.72, 16.5) * mm, v(-36.31, 16.55) * mm, v(-36.58, 16.38) * mm, v(-37.73, 15.23) * mm]});
            skFitSpline(sketch, "E417", {"points": [v(-37.73, 15.23) * mm, v(-38.93, 14.04) * mm, v(-39.01, 13.9) * mm, v(-38.59, 13.83) * mm]});
            skFitSpline(sketch, "E418", {"points": [v(-38.59, 13.83) * mm, v(-38.17, 13.76) * mm, v(-38.1, 13.62) * mm, v(-38.11, 12.76) * mm]});
            skFitSpline(sketch, "E419", {"points": [v(-38.11, 12.76) * mm, v(-38.12, 12.21) * mm, v(-38.4, 10.97) * mm, v(-38.75, 9.98) * mm]});
            skFitSpline(sketch, "E420", {"points": [v(-38.75, 9.98) * mm, v(-39.51, 7.8) * mm, v(-39.52, 7.37) * mm, v(-38.83, 5.2) * mm]});
            skFitSpline(sketch, "E421", {"points": [v(-38.83, 5.2) * mm, v(-38.38, 3.8) * mm, v(-38.3, 3.15) * mm, v(-38.32, 1.4) * mm]});
            skFitSpline(sketch, "E422", {"points": [v(-38.32, 1.4) * mm, v(-38.34, 0.23) * mm, v(-38.26, -1.1) * mm, v(-38.13, -1.57) * mm]});
            skFitSpline(sketch, "E423", {"points": [v(-38.13, -1.57) * mm, v(-37.77, -2.92) * mm, v(-37.86, -6.07) * mm, v(-38.34, -8.88) * mm]});
            skFitSpline(sketch, "E424", {"points": [v(-38.34, -8.88) * mm, v(-38.63, -10.58) * mm, v(-38.76, -12.12) * mm, v(-38.71, -13.3) * mm]});
            skFitSpline(sketch, "E425", {"points": [v(-38.71, -13.3) * mm, v(-38.65, -14.92) * mm, v(-38.56, -15.24) * mm, v(-37.96, -16.18) * mm]});
            skFitSpline(sketch, "E426", {"points": [v(-37.41, -20.41) * mm, v(-37.55, -24.06) * mm, v(-37.43, -24.65) * mm, v(-36.22, -26.18) * mm]});
            skFitSpline(sketch, "E427", {"points": [v(-36.22, -26.18) * mm, v(-34.5, -28.36) * mm, v(-33.66, -30.2) * mm, v(-33.66, -31.8) * mm]});
            skFitSpline(sketch, "E428", {"points": [v(-33.66, -31.8) * mm, v(-33.66, -32.5) * mm, v(-33.82, -32.8) * mm, v(-34.62, -33.66) * mm]});
            skFitSpline(sketch, "E429", {"points": [v(-34.62, -33.66) * mm, v(-35.46, -34.56) * mm, v(-35.57, -34.79) * mm, v(-35.57, -35.64) * mm]});
            skFitSpline(sketch, "E430", {"points": [v(-35.57, -35.64) * mm, v(-35.57, -36.85) * mm, v(-35.16, -37.86) * mm, v(-34.2, -38.96) * mm]});
            skFitSpline(sketch, "E431", {"points": [v(-34.2, -38.96) * mm, v(-33.8, -39.44) * mm, v(-33.28, -40.4) * mm, v(-33.04, -41.1) * mm]});
            skFitSpline(sketch, "E432", {"points": [v(-33.04, -41.1) * mm, v(-32.76, -41.93) * mm, v(-32.24, -42.8) * mm, v(-31.56, -43.59) * mm]});
            skFitSpline(sketch, "E433", {"points": [v(-31.56, -43.59) * mm, v(-29.64, -45.8) * mm, v(-29.61, -45.88) * mm, v(-29.6, -49.55) * mm]});
            skFitSpline(sketch, "E434", {"points": [v(-29.6, -49.55) * mm, v(-29.59, -51.33) * mm, v(-29.65, -53.1) * mm, v(-29.74, -53.47) * mm]});
            skFitSpline(sketch, "E435", {"points": [v(-29.74, -53.47) * mm, v(-29.87, -54.05) * mm, v(-29.78, -54.34) * mm, v(-29.2, -55.24) * mm]});
            skFitSpline(sketch, "E436", {"points": [v(-29.2, -55.24) * mm, v(-28.02, -57.1) * mm, v(-28.34, -58.63) * mm, v(-30.4, -60.92) * mm]});
            skFitSpline(sketch, "E437", {"points": [v(-30.9, -63.02) * mm, v(-30.62, -63.56) * mm, v(-29.54, -65.09) * mm, v(-28.5, -66.4) * mm]});
            skFitSpline(sketch, "E438", {"points": [v(-28.5, -66.4) * mm, v(-27.47, -67.73) * mm, v(-25.87, -70.02) * mm, v(-24.93, -71.5) * mm]});
            skFitSpline(sketch, "E439", {"points": [v(-24.93, -71.5) * mm, v(-21.66, -76.64) * mm, v(-20.53, -77.82) * mm, v(-18.3, -78.38) * mm]});
            skFitSpline(sketch, "E440", {"points": [v(-18.3, -78.38) * mm, v(-17.5, -78.58) * mm, v(-15.88, -79.13) * mm, v(-14.72, -79.6) * mm]});
            skFitSpline(sketch, "E441", {"points": [v(-14.72, -79.6) * mm, v(-13.56, -80.07) * mm, v(-12.22, -80.53) * mm, v(-11.76, -80.63) * mm]});
            skFitSpline(sketch, "E442", {"points": [v(-11.76, -80.63) * mm, v(-10.67, -80.86) * mm, v(-8.14, -80.7) * mm, v(-6.84, -80.3) * mm]});
            skFitSpline(sketch, "E443", {"points": [v(-34.5, 19.17) * mm, v(-34.65, 19.34) * mm, v(-35.11, 19.55) * mm, v(-35.54, 19.62) * mm]});
            skFitSpline(sketch, "E444", {"points": [v(-35.54, 19.62) * mm, v(-35.99, 19.7) * mm, v(-36.79, 20.15) * mm, v(-37.44, 20.68) * mm]});
            skFitSpline(sketch, "E445", {"points": [v(-37.44, 20.68) * mm, v(-38.07, 21.2) * mm, v(-38.96, 21.72) * mm, v(-39.42, 21.86) * mm]});
            skFitSpline(sketch, "E446", {"points": [v(-39.42, 21.86) * mm, v(-39.89, 22) * mm, v(-40.41, 22.34) * mm, v(-40.6, 22.6) * mm]});
            skFitSpline(sketch, "E447", {"points": [v(-40.6, 22.6) * mm, v(-40.88, 23.06) * mm, v(-40.88, 23.2) * mm, v(-40.52, 24.1) * mm]});
            skFitSpline(sketch, "E448", {"points": [v(-40.52, 24.1) * mm, v(-39.98, 25.46) * mm, v(-39.97, 28.27) * mm, v(-40.5, 29.07) * mm]});
            skFitSpline(sketch, "E449", {"points": [v(-40.5, 29.07) * mm, v(-40.94, 29.76) * mm, v(-40.96, 30.33) * mm, v(-40.55, 31.12) * mm]});
            skFitSpline(sketch, "E450", {"points": [v(-40.55, 31.12) * mm, v(-40.35, 31.5) * mm, v(-40.29, 32) * mm, v(-40.37, 32.52) * mm]});
            skFitSpline(sketch, "E451", {"points": [v(-40.37, 32.52) * mm, v(-40.49, 33.2) * mm, v(-40.43, 33.39) * mm, v(-39.97, 33.76) * mm]});
            skFitSpline(sketch, "E452", {"points": [v(-39.97, 33.76) * mm, v(-39.45, 34.2) * mm, v(-38.12, 36.16) * mm, v(-37.84, 36.9) * mm]});
            skFitSpline(sketch, "E453", {"points": [v(-37.84, 36.9) * mm, v(-37.74, 37.17) * mm, v(-37.47, 37.27) * mm, v(-36.87, 37.27) * mm]});
            skFitSpline(sketch, "E454", {"points": [v(-36.87, 37.27) * mm, v(-36.4, 37.27) * mm, v(-35.93, 37.4) * mm, v(-35.78, 37.6) * mm]});
            skFitSpline(sketch, "E455", {"points": [v(-35.78, 37.6) * mm, v(-35.64, 37.77) * mm, v(-35.2, 37.9) * mm, v(-34.82, 37.9) * mm]});
            skFitSpline(sketch, "E456", {"points": [v(-34.82, 37.9) * mm, v(-34.13, 37.9) * mm, v(-34.12, 37.9) * mm, v(-34.23, 37.12) * mm]});
            skFitSpline(sketch, "E457", {"points": [v(-34.23, 37.12) * mm, v(-34.47, 35.46) * mm, v(-34.75, 34.75) * mm, v(-35.37, 34.23) * mm]});
            skFitSpline(sketch, "E458", {"points": [v(-35.37, 34.23) * mm, v(-35.99, 33.7) * mm, v(-36, 33.67) * mm, v(-35.67, 33.16) * mm]});
            skFitSpline(sketch, "E459", {"points": [v(-35.67, 33.16) * mm, v(-34.87, 31.95) * mm, v(-36.1, 31.14) * mm, v(-37.5, 31.95) * mm]});
            skFitSpline(sketch, "E460", {"points": [v(-37.5, 31.95) * mm, v(-37.94, 32.2) * mm, v(-38.35, 32.4) * mm, v(-38.4, 32.4) * mm]});
            skFitSpline(sketch, "E461", {"points": [v(-38.4, 32.4) * mm, v(-38.63, 32.4) * mm, v(-38.23, 31.65) * mm, v(-37.44, 30.52) * mm]});
            skFitSpline(sketch, "E462", {"points": [v(-37.44, 30.52) * mm, v(-36.44, 29.1) * mm, v(-36.35, 28.09) * mm, v(-37.16, 27.33) * mm]});
            skFitSpline(sketch, "E463", {"points": [v(-37.16, 27.33) * mm, v(-37.75, 26.77) * mm, v(-37.88, 25.84) * mm, v(-37.36, 25.84) * mm]});
            skFitSpline(sketch, "E464", {"points": [v(-37.36, 25.84) * mm, v(-37.12, 25.84) * mm, v(-37.08, 25.7) * mm, v(-37.18, 25.26) * mm]});
            skFitSpline(sketch, "E465", {"points": [v(-37.18, 25.26) * mm, v(-37.37, 24.47) * mm, v(-37.66, 23.94) * mm, v(-37.9, 23.94) * mm]});
            skFitSpline(sketch, "E466", {"points": [v(-37.9, 23.94) * mm, v(-38.25, 23.94) * mm, v(-38.13, 23.18) * mm, v(-37.73, 22.82) * mm]});
            skFitSpline(sketch, "E467", {"points": [v(-37.73, 22.82) * mm, v(-37.52, 22.63) * mm, v(-36.88, 22.27) * mm, v(-36.3, 22.02) * mm]});
            skFitSpline(sketch, "E468", {"points": [v(-36.3, 22.02) * mm, v(-33.61, 20.87) * mm, v(-33.45, 20.76) * mm, v(-33.45, 20.13) * mm]});
            skFitSpline(sketch, "E469", {"points": [v(-33.45, 20.13) * mm, v(-33.45, 18.94) * mm, v(-33.94, 18.5) * mm, v(-34.5, 19.17) * mm]});
            skFitSpline(sketch, "E470", {"points": [v(-33.88, 20.11) * mm, v(-33.88, 20.2) * mm, v(-34.7, 20.65) * mm, v(-35.7, 21.1) * mm]});
            skFitSpline(sketch, "E471", {"points": [v(-35.7, 21.1) * mm, v(-38.2, 22.21) * mm, v(-38.53, 22.5) * mm, v(-38.53, 23.53) * mm]});
            skFitSpline(sketch, "E472", {"points": [v(-38.53, 23.53) * mm, v(-38.53, 23.99) * mm, v(-38.45, 24.36) * mm, v(-38.35, 24.36) * mm]});
            skFitSpline(sketch, "E473", {"points": [v(-38.35, 24.36) * mm, v(-38.26, 24.36) * mm, v(-38.08, 24.58) * mm, v(-37.96, 24.84) * mm]});
            skFitSpline(sketch, "E474", {"points": [v(-37.96, 24.84) * mm, v(-37.8, 25.2) * mm, v(-37.81, 25.39) * mm, v(-38.03, 25.6) * mm]});
            skFitSpline(sketch, "E475", {"points": [v(-38.03, 25.6) * mm, v(-38.5, 26.03) * mm, v(-38.36, 26.84) * mm, v(-37.67, 27.63) * mm]});
            skFitSpline(sketch, "E476", {"points": [v(-37.67, 27.63) * mm, v(-36.9, 28.51) * mm, v(-36.94, 28.8) * mm, v(-38.14, 30.48) * mm]});
            skFitSpline(sketch, "E477", {"points": [v(-38.14, 30.48) * mm, v(-38.63, 31.17) * mm, v(-38.96, 31.87) * mm, v(-38.96, 32.23) * mm]});
            skFitSpline(sketch, "E478", {"points": [v(-38.96, 32.23) * mm, v(-38.96, 32.75) * mm, v(-38.87, 32.83) * mm, v(-38.36, 32.83) * mm]});
            skFitSpline(sketch, "E479", {"points": [v(-38.36, 32.83) * mm, v(-38.03, 32.83) * mm, v(-37.58, 32.69) * mm, v(-37.36, 32.52) * mm]});
            skFitSpline(sketch, "E480", {"points": [v(-37.36, 32.52) * mm, v(-36.98, 32.23) * mm, v(-36, 32.07) * mm, v(-36, 32.3) * mm]});
            skFitSpline(sketch, "E481", {"points": [v(-36, 32.3) * mm, v(-36, 32.35) * mm, v(-36.15, 32.73) * mm, v(-36.35, 33.14) * mm]});
            skFitSpline(sketch, "E482", {"points": [v(-35.92, 34.57) * mm, v(-35.27, 35.14) * mm, v(-35.1, 35.46) * mm, v(-34.96, 36.38) * mm]});
            skFitSpline(sketch, "E483", {"points": [v(-34.96, 36.38) * mm, v(-34.86, 36.99) * mm, v(-34.82, 37.49) * mm, v(-34.87, 37.49) * mm]});
            skFitSpline(sketch, "E484", {"points": [v(-34.87, 37.49) * mm, v(-34.91, 37.49) * mm, v(-35.23, 37.28) * mm, v(-35.56, 37.04) * mm]});
            skFitSpline(sketch, "E485", {"points": [v(-35.56, 37.04) * mm, v(-35.96, 36.74) * mm, v(-36.36, 36.62) * mm, v(-36.72, 36.69) * mm]});
            skFitSpline(sketch, "E486", {"points": [v(-36.72, 36.69) * mm, v(-37.02, 36.75) * mm, v(-37.26, 36.72) * mm, v(-37.26, 36.64) * mm]});
            skFitSpline(sketch, "E487", {"points": [v(-37.26, 36.64) * mm, v(-37.26, 36.35) * mm, v(-39.4, 33.25) * mm, v(-39.6, 33.25) * mm]});
            skFitSpline(sketch, "E488", {"points": [v(-39.6, 33.25) * mm, v(-39.71, 33.25) * mm, v(-39.8, 32.75) * mm, v(-39.8, 32.14) * mm]});
            skFitSpline(sketch, "E489", {"points": [v(-39.8, 32.14) * mm, v(-39.81, 31.5) * mm, v(-39.95, 30.86) * mm, v(-40.13, 30.62) * mm]});
            skFitSpline(sketch, "E490", {"points": [v(-40.13, 30.62) * mm, v(-40.4, 30.26) * mm, v(-40.4, 30.15) * mm, v(-40.08, 29.67) * mm]});
            skFitSpline(sketch, "E491", {"points": [v(-40.08, 29.67) * mm, v(-39.54, 28.86) * mm, v(-39.43, 25.58) * mm, v(-39.9, 24.18) * mm]});
            skFitSpline(sketch, "E492", {"points": [v(-39.9, 24.18) * mm, v(-40.1, 23.59) * mm, v(-40.2, 23.02) * mm, v(-40.14, 22.92) * mm]});
            skFitSpline(sketch, "E493", {"points": [v(-40.14, 22.92) * mm, v(-40.08, 22.82) * mm, v(-39.57, 22.56) * mm, v(-39.02, 22.35) * mm]});
            skFitSpline(sketch, "E494", {"points": [v(-39.02, 22.35) * mm, v(-38.46, 22.15) * mm, v(-37.5, 21.56) * mm, v(-36.87, 21.05) * mm]});
            skFitSpline(sketch, "E495", {"points": [v(-36.87, 21.05) * mm, v(-36.12, 20.45) * mm, v(-35.53, 20.13) * mm, v(-35.13, 20.13) * mm]});
            skFitSpline(sketch, "E496", {"points": [v(-35.13, 20.13) * mm, v(-34.8, 20.13) * mm, v(-34.48, 20.03) * mm, v(-34.4, 19.91) * mm]});
            skFitSpline(sketch, "E497", {"points": [v(-34.4, 19.91) * mm, v(-34.26, 19.68) * mm, v(-33.88, 19.83) * mm, v(-33.88, 20.11) * mm]});
            skFitSpline(sketch, "E498", {"points": [v(-35.84, 27.25) * mm, v(-35.9, 27.35) * mm, v(-36.01, 27.96) * mm, v(-36.1, 28.6) * mm]});
            skFitSpline(sketch, "E499", {"points": [v(-36.1, 28.6) * mm, v(-36.27, 30.1) * mm, v(-35.9, 30.72) * mm, v(-35.07, 30.34) * mm]});
            skFitSpline(sketch, "E500", {"points": [v(-35.07, 30.34) * mm, v(-34.7, 30.18) * mm, v(-34.56, 29.98) * mm, v(-34.64, 29.77) * mm]});
            skFitSpline(sketch, "E501", {"points": [v(-34.64, 29.77) * mm, v(-34.74, 29.52) * mm, v(-34.61, 29.44) * mm, v(-34.1, 29.44) * mm]});
            skFitSpline(sketch, "E502", {"points": [v(-34.1, 29.44) * mm, v(-33.14, 29.44) * mm, v(-32.6, 29.1) * mm, v(-32.6, 28.48) * mm]});
            skFitSpline(sketch, "E503", {"points": [v(-32.6, 28.48) * mm, v(-32.6, 28.2) * mm, v(-32.71, 27.96) * mm, v(-32.85, 27.96) * mm]});
            skFitSpline(sketch, "E504", {"points": [v(-32.85, 27.96) * mm, v(-32.98, 27.96) * mm, v(-33.2, 27.8) * mm, v(-33.34, 27.62) * mm]});
            skFitSpline(sketch, "E505", {"points": [v(-33.34, 27.62) * mm, v(-33.62, 27.24) * mm, v(-35.65, 26.94) * mm, v(-35.84, 27.25) * mm]});
            skFitSpline(sketch, "E506", {"points": [v(-33.88, 28.07) * mm, v(-33.88, 28.24) * mm, v(-33.73, 28.38) * mm, v(-33.56, 28.38) * mm]});
            skFitSpline(sketch, "E507", {"points": [v(-33.56, 28.38) * mm, v(-33.38, 28.38) * mm, v(-33.24, 28.48) * mm, v(-33.24, 28.6) * mm]});
            skFitSpline(sketch, "E508", {"points": [v(-33.24, 28.6) * mm, v(-33.24, 28.71) * mm, v(-33.73, 28.8) * mm, v(-34.32, 28.8) * mm]});
            skFitSpline(sketch, "E509", {"points": [v(-34.32, 28.8) * mm, v(-35.4, 28.8) * mm, v(-35.4, 28.81) * mm, v(-35.31, 29.43) * mm]});
            skFitSpline(sketch, "E510", {"points": [v(-35.31, 29.43) * mm, v(-35.26, 29.77) * mm, v(-35.3, 30) * mm, v(-35.4, 29.95) * mm]});
            skFitSpline(sketch, "E511", {"points": [v(-35.4, 29.95) * mm, v(-35.6, 29.82) * mm, v(-35.62, 28.91) * mm, v(-35.44, 28.23) * mm]});
            skFitSpline(sketch, "E512", {"points": [v(-35.44, 28.23) * mm, v(-35.33, 27.85) * mm, v(-35.16, 27.75) * mm, v(-34.6, 27.75) * mm]});
            skFitSpline(sketch, "E513", {"points": [v(-34.6, 27.75) * mm, v(-34.1, 27.75) * mm, v(-33.88, 27.85) * mm, v(-33.88, 28.07) * mm]});
            skFitSpline(sketch, "E514", {"points": [v(-34.5, 30.49) * mm, v(-34.87, 31.18) * mm, v(-34.75, 31.97) * mm, v(-34.2, 32.53) * mm]});
            skFitSpline(sketch, "E515", {"points": [v(-34.2, 32.53) * mm, v(-33.9, 32.82) * mm, v(-33.66, 33.2) * mm, v(-33.66, 33.37) * mm]});
            skFitSpline(sketch, "E516", {"points": [v(-33.66, 33.37) * mm, v(-33.66, 33.54) * mm, v(-33.57, 33.68) * mm, v(-33.45, 33.68) * mm]});
            skFitSpline(sketch, "E517", {"points": [v(-33.45, 33.68) * mm, v(-33.34, 33.68) * mm, v(-33.24, 33.6) * mm, v(-33.24, 33.51) * mm]});
            skFitSpline(sketch, "E518", {"points": [v(-33.24, 33.51) * mm, v(-33.24, 33.42) * mm, v(-32.95, 33.24) * mm, v(-32.6, 33.1) * mm]});
            skFitSpline(sketch, "E519", {"points": [v(-32.6, 33.1) * mm, v(-31.72, 32.77) * mm, v(-31.8, 32.27) * mm, v(-32.94, 31.08) * mm]});
            skFitSpline(sketch, "E520", {"points": [v(-32.94, 31.08) * mm, v(-34, 29.96) * mm, v(-34.19, 29.9) * mm, v(-34.5, 30.49) * mm]});
            skFitSpline(sketch, "E521", {"points": [v(-32.6, 32.45) * mm, v(-32.6, 32.54) * mm, v(-32.75, 32.62) * mm, v(-32.92, 32.62) * mm]});
            skFitSpline(sketch, "E522", {"points": [v(-32.92, 32.62) * mm, v(-33.1, 32.62) * mm, v(-33.24, 32.53) * mm, v(-33.24, 32.43) * mm]});
            skFitSpline(sketch, "E523", {"points": [v(-33.24, 32.43) * mm, v(-33.24, 32.33) * mm, v(-33.43, 32.2) * mm, v(-33.66, 32.13) * mm]});
            skFitSpline(sketch, "E524", {"points": [v(-33.66, 32.13) * mm, v(-33.96, 32.06) * mm, v(-34.09, 31.84) * mm, v(-34.09, 31.43) * mm]});
            skFitSpline(sketch, "E525", {"points": [v(-33.35, 31.56) * mm, v(-32.94, 31.95) * mm, v(-32.6, 32.35) * mm, v(-32.6, 32.45) * mm]});
            skSolve(sketch);
        }
        {
            var Q0;
            Q0=makeQuery(id+"F0.imprint","IMPRINT",FACE,{"disambiguationData":[TD([[makeQuery(id+"F0.imprint","IMPRINT",EDGE,{"derivedFrom":sQuery(id+"F0.wireOp",EDGE,"E12")}),1.0]])]});
            var Q1;
            Q1=makeQuery(id+"F0.imprint","IMPRINT",FACE,{"disambiguationData":[TD([[makeQuery(id+"F0.imprint","IMPRINT",EDGE,{"derivedFrom":sQuery(id+"F0.wireOp",EDGE,"E26")}),1.0]])]});
            var Q2;
            Q2=makeQuery(id+"F0.imprint","IMPRINT",FACE,{"disambiguationData":[TD([[makeQuery(id+"F0.imprint","IMPRINT",EDGE,{"derivedFrom":sQuery(id+"F0.wireOp",EDGE,"E506")}),1.0]])]});
            var Q3;
            Q3=makeQuery(id+"F0.imprint","IMPRINT",FACE,{"disambiguationData":[TD([[makeQuery(id+"F0.imprint","IMPRINT",EDGE,{"derivedFrom":sQuery(id+"F0.wireOp",EDGE,"E28")}),1.0]])]});
            extrude(context, id + "F1", {"entities" : qUnion([Q0, Q1, Q2, Q3]), "depth" : 3 * mm, "offsetDistance" : 25 * mm});
        }
        {
            var Q0;
            Q0=makeQuery(id+"F1.opExtrude","CAP_FACE",FACE,{"disambiguationData":[OSD([sQuery(id+"F0.wireOp",EDGE,"E12"),sQuery(id+"F0.wireOp",EDGE,"E13"),sQuery(id+"F0.wireOp",EDGE,"E14"),sQuery(id+"F0.wireOp",EDGE,"E15"),sQuery(id+"F0.wireOp",EDGE,"E16"),sQuery(id+"F0.wireOp",EDGE,"E17"),sQuery(id+"F0.wireOp",EDGE,"E18"),sQuery(id+"F0.wireOp",EDGE,"E19"),sQuery(id+"F0.wireOp",EDGE,"E20"),sQuery(id+"F0.wireOp",EDGE,"E21"),sQuery(id+"F0.wireOp",EDGE,"E22"),sQuery(id+"F0.wireOp",EDGE,"E23"),sQuery(id+"F0.wireOp",EDGE,"E24"),sQuery(id+"F0.wireOp",EDGE,"E25"),sQuery(id+"F0.wireOp",EDGE,"E233"),sQuery(id+"F0.wireOp",EDGE,"E234"),sQuery(id+"F0.wireOp",EDGE,"E235"),sQuery(id+"F0.wireOp",EDGE,"E236"),sQuery(id+"F0.wireOp",EDGE,"E237"),sQuery(id+"F0.wireOp",EDGE,"E238"),sQuery(id+"F0.wireOp",EDGE,"E239"),sQuery(id+"F0.wireOp",EDGE,"E240"),sQuery(id+"F0.wireOp",EDGE,"E241"),sQuery(id+"F0.wireOp",EDGE,"E242"),sQuery(id+"F0.wireOp",EDGE,"E243"),sQuery(id+"F0.wireOp",EDGE,"E244"),sQuery(id+"F0.wireOp",EDGE,"E245"),sQuery(id+"F0.wireOp",EDGE,"E246"),sQuery(id+"F0.wireOp",EDGE,"E247"),sQuery(id+"F0.wireOp",EDGE,"E248"),sQuery(id+"F0.wireOp",EDGE,"E249"),sQuery(id+"F0.wireOp",EDGE,"E250"),sQuery(id+"F0.wireOp",EDGE,"E251"),sQuery(id+"F0.wireOp",EDGE,"E252"),sQuery(id+"F0.wireOp",EDGE,"E253"),sQuery(id+"F0.wireOp",EDGE,"E254"),sQuery(id+"F0.wireOp",EDGE,"E255"),sQuery(id+"F0.wireOp",EDGE,"E256"),sQuery(id+"F0.wireOp",EDGE,"E257"),sQuery(id+"F0.wireOp",EDGE,"E258"),sQuery(id+"F0.wireOp",EDGE,"E259"),sQuery(id+"F0.wireOp",EDGE,"E260"),sQuery(id+"F0.wireOp",EDGE,"E261"),sQuery(id+"F0.wireOp",EDGE,"E262"),sQuery(id+"F0.wireOp",EDGE,"E263"),sQuery(id+"F0.wireOp",EDGE,"E264"),sQuery(id+"F0.wireOp",EDGE,"E265"),sQuery(id+"F0.wireOp",EDGE,"E266"),sQuery(id+"F0.wireOp",EDGE,"E267"),sQuery(id+"F0.wireOp",EDGE,"E268"),sQuery(id+"F0.wireOp",EDGE,"E269"),sQuery(id+"F0.wireOp",EDGE,"E270"),sQuery(id+"F0.wireOp",EDGE,"E271"),sQuery(id+"F0.wireOp",EDGE,"E272"),sQuery(id+"F0.wireOp",EDGE,"E273"),sQuery(id+"F0.wireOp",EDGE,"E274"),sQuery(id+"F0.wireOp",EDGE,"E275"),sQuery(id+"F0.wireOp",EDGE,"E276"),sQuery(id+"F0.wireOp",EDGE,"E277"),sQuery(id+"F0.wireOp",EDGE,"E278"),sQuery(id+"F0.wireOp",EDGE,"E279"),sQuery(id+"F0.wireOp",EDGE,"E280"),sQuery(id+"F0.wireOp",EDGE,"E281"),sQuery(id+"F0.wireOp",EDGE,"E282"),sQuery(id+"F0.wireOp",EDGE,"E283"),sQuery(id+"F0.wireOp",EDGE,"E284"),sQuery(id+"F0.wireOp",EDGE,"E285"),sQuery(id+"F0.wireOp",EDGE,"E286"),sQuery(id+"F0.wireOp",EDGE,"E287"),sQuery(id+"F0.wireOp",EDGE,"E288"),sQuery(id+"F0.wireOp",EDGE,"E289"),sQuery(id+"F0.wireOp",EDGE,"E290"),sQuery(id+"F0.wireOp",EDGE,"E291"),sQuery(id+"F0.wireOp",EDGE,"E292"),sQuery(id+"F0.wireOp",EDGE,"E293"),sQuery(id+"F0.wireOp",EDGE,"E294"),sQuery(id+"F0.wireOp",EDGE,"E295"),sQuery(id+"F0.wireOp",EDGE,"E296"),sQuery(id+"F0.wireOp",EDGE,"E297"),sQuery(id+"F0.wireOp",EDGE,"E298"),sQuery(id+"F0.wireOp",EDGE,"E299"),sQuery(id+"F0.wireOp",EDGE,"E300"),sQuery(id+"F0.wireOp",EDGE,"E301"),sQuery(id+"F0.wireOp",EDGE,"E302"),sQuery(id+"F0.wireOp",EDGE,"E303"),sQuery(id+"F0.wireOp",EDGE,"E304"),sQuery(id+"F0.wireOp",EDGE,"E305"),sQuery(id+"F0.wireOp",EDGE,"E306"),sQuery(id+"F0.wireOp",EDGE,"E307"),sQuery(id+"F0.wireOp",EDGE,"E308"),sQuery(id+"F0.wireOp",EDGE,"E309"),sQuery(id+"F0.wireOp",EDGE,"E310"),sQuery(id+"F0.wireOp",EDGE,"E311"),sQuery(id+"F0.wireOp",EDGE,"E312"),sQuery(id+"F0.wireOp",EDGE,"E313"),sQuery(id+"F0.wireOp",EDGE,"E314"),sQuery(id+"F0.wireOp",EDGE,"E315"),sQuery(id+"F0.wireOp",EDGE,"E316"),sQuery(id+"F0.wireOp",EDGE,"E317"),sQuery(id+"F0.wireOp",EDGE,"E318"),sQuery(id+"F0.wireOp",EDGE,"E319"),sQuery(id+"F0.wireOp",EDGE,"E320"),sQuery(id+"F0.wireOp",EDGE,"E321"),sQuery(id+"F0.wireOp",EDGE,"E322"),sQuery(id+"F0.wireOp",EDGE,"E323"),sQuery(id+"F0.wireOp",EDGE,"E324"),sQuery(id+"F0.wireOp",EDGE,"E325"),sQuery(id+"F0.wireOp",EDGE,"E326"),sQuery(id+"F0.wireOp",EDGE,"E327"),sQuery(id+"F0.wireOp",EDGE,"E328"),sQuery(id+"F0.wireOp",EDGE,"E329"),sQuery(id+"F0.wireOp",EDGE,"E330"),sQuery(id+"F0.wireOp",EDGE,"E331"),sQuery(id+"F0.wireOp",EDGE,"E332"),sQuery(id+"F0.wireOp",EDGE,"E333"),sQuery(id+"F0.wireOp",EDGE,"E334"),sQuery(id+"F0.wireOp",EDGE,"E335"),sQuery(id+"F0.wireOp",EDGE,"E336"),sQuery(id+"F0.wireOp",EDGE,"E337"),sQuery(id+"F0.wireOp",EDGE,"E338"),sQuery(id+"F0.wireOp",EDGE,"E339"),sQuery(id+"F0.wireOp",EDGE,"E340"),sQuery(id+"F0.wireOp",EDGE,"E341"),sQuery(id+"F0.wireOp",EDGE,"E342"),sQuery(id+"F0.wireOp",EDGE,"E343"),sQuery(id+"F0.wireOp",EDGE,"E344"),sQuery(id+"F0.wireOp",EDGE,"E345"),sQuery(id+"F0.wireOp",EDGE,"E346"),sQuery(id+"F0.wireOp",EDGE,"E347"),sQuery(id+"F0.wireOp",EDGE,"E348"),sQuery(id+"F0.wireOp",EDGE,"E349"),sQuery(id+"F0.wireOp",EDGE,"E350"),sQuery(id+"F0.wireOp",EDGE,"E351"),sQuery(id+"F0.wireOp",EDGE,"E352"),sQuery(id+"F0.wireOp",EDGE,"E353"),sQuery(id+"F0.wireOp",EDGE,"E354"),sQuery(id+"F0.wireOp",EDGE,"E355"),sQuery(id+"F0.wireOp",EDGE,"E356"),sQuery(id+"F0.wireOp",EDGE,"E357"),sQuery(id+"F0.wireOp",EDGE,"E358"),sQuery(id+"F0.wireOp",EDGE,"E359"),sQuery(id+"F0.wireOp",EDGE,"E360"),sQuery(id+"F0.wireOp",EDGE,"E361"),sQuery(id+"F0.wireOp",EDGE,"E362"),sQuery(id+"F0.wireOp",EDGE,"E363"),sQuery(id+"F0.wireOp",EDGE,"E364"),sQuery(id+"F0.wireOp",EDGE,"E365"),sQuery(id+"F0.wireOp",EDGE,"E366"),sQuery(id+"F0.wireOp",EDGE,"E367"),sQuery(id+"F0.wireOp",EDGE,"E368"),sQuery(id+"F0.wireOp",EDGE,"E369"),sQuery(id+"F0.wireOp",EDGE,"E370"),sQuery(id+"F0.wireOp",EDGE,"E371"),sQuery(id+"F0.wireOp",EDGE,"E372"),sQuery(id+"F0.wireOp",EDGE,"E373"),sQuery(id+"F0.wireOp",EDGE,"E374"),sQuery(id+"F0.wireOp",EDGE,"E375"),sQuery(id+"F0.wireOp",EDGE,"E376"),sQuery(id+"F0.wireOp",EDGE,"E377"),sQuery(id+"F0.wireOp",EDGE,"E378"),sQuery(id+"F0.wireOp",EDGE,"E379"),sQuery(id+"F0.wireOp",EDGE,"E380"),sQuery(id+"F0.wireOp",EDGE,"E381"),sQuery(id+"F0.wireOp",EDGE,"E382"),sQuery(id+"F0.wireOp",EDGE,"E383"),sQuery(id+"F0.wireOp",EDGE,"E384"),sQuery(id+"F0.wireOp",EDGE,"E385"),sQuery(id+"F0.wireOp",EDGE,"E386"),sQuery(id+"F0.wireOp",EDGE,"E387"),sQuery(id+"F0.wireOp",EDGE,"E388"),sQuery(id+"F0.wireOp",EDGE,"E389"),sQuery(id+"F0.wireOp",EDGE,"E390"),sQuery(id+"F0.wireOp",EDGE,"E391"),sQuery(id+"F0.wireOp",EDGE,"E392"),sQuery(id+"F0.wireOp",EDGE,"E393"),sQuery(id+"F0.wireOp",EDGE,"E394"),sQuery(id+"F0.wireOp",EDGE,"E395"),sQuery(id+"F0.wireOp",EDGE,"E396"),sQuery(id+"F0.wireOp",EDGE,"E397"),sQuery(id+"F0.wireOp",EDGE,"E398"),sQuery(id+"F0.wireOp",EDGE,"E399"),sQuery(id+"F0.wireOp",EDGE,"E400"),sQuery(id+"F0.wireOp",EDGE,"E401"),sQuery(id+"F0.wireOp",EDGE,"E402"),sQuery(id+"F0.wireOp",EDGE,"E403"),sQuery(id+"F0.wireOp",EDGE,"E404"),sQuery(id+"F0.wireOp",EDGE,"E405"),sQuery(id+"F0.wireOp",EDGE,"E406"),sQuery(id+"F0.wireOp",EDGE,"E407"),sQuery(id+"F0.wireOp",EDGE,"E408"),sQuery(id+"F0.wireOp",EDGE,"E409"),sQuery(id+"F0.wireOp",EDGE,"E410"),sQuery(id+"F0.wireOp",EDGE,"E411"),sQuery(id+"F0.wireOp",EDGE,"E412"),sQuery(id+"F0.wireOp",EDGE,"E413"),sQuery(id+"F0.wireOp",EDGE,"E414"),sQuery(id+"F0.wireOp",EDGE,"E415"),sQuery(id+"F0.wireOp",EDGE,"E416"),sQuery(id+"F0.wireOp",EDGE,"E417"),sQuery(id+"F0.wireOp",EDGE,"E418"),sQuery(id+"F0.wireOp",EDGE,"E419"),sQuery(id+"F0.wireOp",EDGE,"E420"),sQuery(id+"F0.wireOp",EDGE,"E421"),sQuery(id+"F0.wireOp",EDGE,"E422"),sQuery(id+"F0.wireOp",EDGE,"E423"),sQuery(id+"F0.wireOp",EDGE,"E424"),sQuery(id+"F0.wireOp",EDGE,"E425"),sQuery(id+"F0.wireOp",EDGE,"E426"),sQuery(id+"F0.wireOp",EDGE,"E427"),sQuery(id+"F0.wireOp",EDGE,"E428"),sQuery(id+"F0.wireOp",EDGE,"E429"),sQuery(id+"F0.wireOp",EDGE,"E430"),sQuery(id+"F0.wireOp",EDGE,"E431"),sQuery(id+"F0.wireOp",EDGE,"E432"),sQuery(id+"F0.wireOp",EDGE,"E433"),sQuery(id+"F0.wireOp",EDGE,"E434"),sQuery(id+"F0.wireOp",EDGE,"E435"),sQuery(id+"F0.wireOp",EDGE,"E436"),sQuery(id+"F0.wireOp",EDGE,"E437"),sQuery(id+"F0.wireOp",EDGE,"E438"),sQuery(id+"F0.wireOp",EDGE,"E439"),sQuery(id+"F0.wireOp",EDGE,"E440"),sQuery(id+"F0.wireOp",EDGE,"E441"),sQuery(id+"F0.wireOp",EDGE,"E442")])],"isStart":false});
            var sketch = newSketch(context, id + "F2", { "sketchPlane" : qUnion([Q0])});
            skLineSegment(sketch, "E526", {"start": v(-18.12, 52.26) * mm, "end": v(-2.72, 52.26) * mm});
            skLineSegment(sketch, "E527", {"start": v(-2.72, 52.26) * mm, "end": v(-2.72, 57.25) * mm});
            skLineSegment(sketch, "E528", {"start": v(-2.72, 57.25) * mm, "end": v(9.81, 57.25) * mm});
            skLineSegment(sketch, "E529", {"start": v(9.81, 57.25) * mm, "end": v(9.81, 54.32) * mm});
            skLineSegment(sketch, "E530", {"start": v(9.81, 54.32) * mm, "end": v(15.66, 54.32) * mm});
            skLineSegment(sketch, "E531", {"start": v(15.66, 54.32) * mm, "end": v(15.66, 46.72) * mm});
            skLineSegment(sketch, "E532", {"start": v(15.66, 46.72) * mm, "end": v(7.64, 37.18) * mm});
            skLineSegment(sketch, "E533", {"start": v(7.64, 37.18) * mm, "end": v(-2.52, 37.18) * mm});
            skLineSegment(sketch, "E534", {"start": v(-2.52, 37.18) * mm, "end": v(-2.52, 39.55) * mm});
            skLineSegment(sketch, "E535", {"start": v(-2.52, 39.55) * mm, "end": v(-24.5, 39.55) * mm});
            skLineSegment(sketch, "E536", {"start": v(15.66, 51.29) * mm, "end": v(21.38, 51.29) * mm});
            skLineSegment(sketch, "E537", {"start": v(21.38, 51.29) * mm, "end": v(21.38, 60.62) * mm});
            skLineSegment(sketch, "E538", {"start": v(7.64, 37.18) * mm, "end": v(7.64, 29.75) * mm});
            skLineSegment(sketch, "E539", {"start": v(7.64, 29.75) * mm, "end": v(12.1, 22.91) * mm});
            skLineSegment(sketch, "E540", {"start": v(12.1, 22.91) * mm, "end": v(27.69, 22.91) * mm});
            skLineSegment(sketch, "E541", {"start": v(12.1, 22.91) * mm, "end": v(12.1, 16.76) * mm});
            skLineSegment(sketch, "E542", {"start": v(12.1, 16.76) * mm, "end": v(1.97, 16.76) * mm});
            skLineSegment(sketch, "E543", {"start": v(1.97, 16.76) * mm, "end": v(-2.49, 11.93) * mm});
            skLineSegment(sketch, "E544", {"start": v(-2.49, 11.93) * mm, "end": v(-2.49, -5.73) * mm});
            skLineSegment(sketch, "E545", {"start": v(-2.49, -5.73) * mm, "end": v(-11.22, -5.73) * mm});
            skLineSegment(sketch, "E546", {"start": v(-11.22, -5.73) * mm, "end": v(-11.22, -20.41) * mm});
            skLineSegment(sketch, "E547", {"start": v(-11.22, -20.41) * mm, "end": v(-37.41, -20.41) * mm});
            skLineSegment(sketch, "E548", {"start": v(12.1, 16.76) * mm, "end": v(12.1, 6.9) * mm});
            skLineSegment(sketch, "E549", {"start": v(12.1, 6.9) * mm, "end": v(20, 4.1) * mm});
            skLineSegment(sketch, "E550", {"start": v(20, 4.1) * mm, "end": v(21.49, 1.6) * mm});
            skLineSegment(sketch, "E551", {"start": v(21.49, 1.6) * mm, "end": v(30.51, 5.43) * mm});
            skLineSegment(sketch, "E552", {"start": v(-2.49, -1.8) * mm, "end": v(10.7, -1.8) * mm});
            skLineSegment(sketch, "E553", {"start": v(10.7, -1.8) * mm, "end": v(15.13, -16.6) * mm});
            skLineSegment(sketch, "E554", {"start": v(15.13, -16.6) * mm, "end": v(7.17, -21.46) * mm});
            skLineSegment(sketch, "E555", {"start": v(7.17, -21.46) * mm, "end": v(22.2, -30.75) * mm});
            skLineSegment(sketch, "E556", {"start": v(22.2, -30.75) * mm, "end": v(22.2, -20.3) * mm});
            skLineSegment(sketch, "E557", {"start": v(22.2, -20.3) * mm, "end": v(33.62, -14.84) * mm});
            skLineSegment(sketch, "E558", {"start": v(33.62, -14.84) * mm, "end": v(31.3, -9.96) * mm});
            skLineSegment(sketch, "E559", {"start": v(31.3, -9.96) * mm, "end": v(30.12, -10.51) * mm});
            skLineSegment(sketch, "E560", {"start": v(30.12, -10.51) * mm, "end": v(23.86, 2.6) * mm});
            skLineSegment(sketch, "E561", {"start": v(14.68, -26.1) * mm, "end": v(14.68, -60.19) * mm});
            skLineSegment(sketch, "E562", {"start": v(14.68, -60.19) * mm, "end": v(26.57, -60.19) * mm});
            skArc(sketch, "E563", {"start": v(37.7, -11.18) * mm, "mid": v(34.3, -11.48) * mm, "end": v(33.62, -14.84) * mm});
            skSolve(sketch);
        }
        {
            var Q0;
            Q0=makeQuery(id+"F2.imprint","IMPRINT",FACE,{"disambiguationData":[TD([[makeQuery(id+"F2.imprint","IMPRINT",EDGE,{"derivedFrom":sQuery(id+"F2.wireOp",EDGE,"E526")}),1.0]])]});
            var Q1;
            Q1=makeQuery(id+"F2.imprint","IMPRINT",FACE,{"disambiguationData":[TD([[makeQuery(id+"F2.imprint","IMPRINT",EDGE,{"derivedFrom":sQuery(id+"F2.wireOp",EDGE,"E526")}),-1.0]])]});
            var Q2;
            {var subQ2=sQuery(id+"F2.wireOp",EDGE,"E532");Q2=makeQuery(id+"F2.imprint","IMPRINT",FACE,{"disambiguationData":[TD([[makeQuery(id+"F2.imprint","IMPRINT",EDGE,{"derivedFrom":subQ2}),1.0]])]});}
            var Q3;
            Q3=makeQuery(id+"F2.imprint","IMPRINT",FACE,{"disambiguationData":[TD([[makeQuery(id+"F2.imprint","IMPRINT",EDGE,{"derivedFrom":sQuery(id+"F2.wireOp",EDGE,"E533")}),1.0]])]});
            var Q4;
            Q4=makeQuery(id+"F2.imprint","IMPRINT",FACE,{"disambiguationData":[TD([[makeQuery(id+"F2.imprint","IMPRINT",EDGE,{"derivedFrom":sQuery(id+"F2.wireOp",EDGE,"E542")}),1.0]])]});
            var Q5;
            {var subQ0=sQuery(id+"F2.wireOp",EDGE,"E540");Q5=makeQuery(id+"F2.imprint","IMPRINT",FACE,{"disambiguationData":[TD([[makeQuery(id+"F2.imprint","IMPRINT",EDGE,{"derivedFrom":subQ0}),-1.0]])]});}
            var Q6;
            Q6=makeQuery(id+"F2.imprint","IMPRINT",FACE,{"disambiguationData":[TD([[makeQuery(id+"F2.imprint","IMPRINT",EDGE,{"derivedFrom":sQuery(id+"F2.wireOp",EDGE,"E558")}),-1.0]])]});
            var Q7;
            {var subQ6=sQuery(id+"F2.wireOp",EDGE,"E545");Q7=makeQuery(id+"F2.imprint","IMPRINT",FACE,{"disambiguationData":[TD([[makeQuery(id+"F2.imprint","IMPRINT",EDGE,{"derivedFrom":subQ6}),1.0]])]});}
            extrude(context, id + "F3", {"entities" : qUnion([Q0, Q1, Q2, Q3, Q4, Q5, Q6, Q7]), "operationType" : NewBodyOperationType.REMOVE, "oppositeDirection" : true, "depth" : 25 * mm, "offsetDistance" : 25 * mm});
        }
    });
